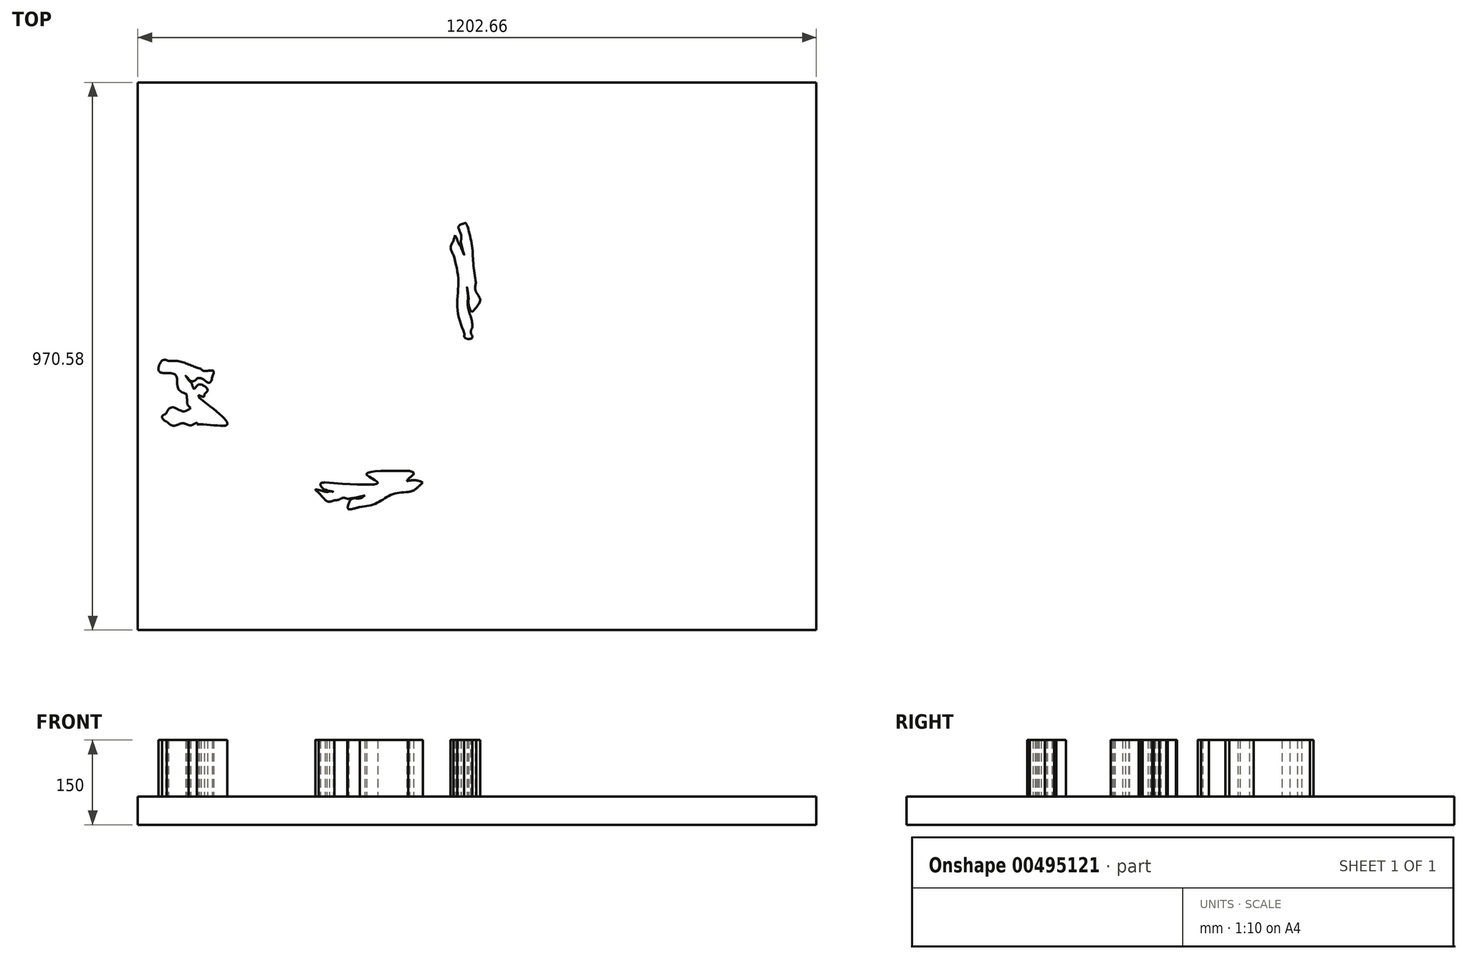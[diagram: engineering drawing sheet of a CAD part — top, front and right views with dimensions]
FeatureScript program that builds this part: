
annotation { "Feature Type Name" : "Feature", "Feature Type Description" : "" }
export const myFeature = defineFeature(function(context is Context, id is Id, definition is map)
    precondition{}
    {
        {
            var Q0;
            Q0=qCreatedBy(makeId("Top.planeOp"),FACE);
            var sketch = newSketch(context, id + "F0", { "sketchPlane" : qUnion([Q0])});
            skFitSpline(sketch, "E0", {"points": [v(381.94, 4384.72) * mm, v(61.51, 4229.76) * mm, v(-168.88, 3941.71) * mm, v(-376.86, 3662.72) * mm]});
            skFitSpline(sketch, "E1", {"points": [v(-376.86, 3662.72) * mm, v(-485.66, 3465.57) * mm, v(-439.05, 3228.77) * mm, v(-451.72, 3017.95) * mm]});
            skFitSpline(sketch, "E2", {"points": [v(-451.72, 3017.95) * mm, v(-592.53, 3305.6) * mm, v(-700.1, 3616.54) * mm, v(-908.92, 3864.94) * mm]});
            skFitSpline(sketch, "E3", {"points": [v(-908.92, 3864.94) * mm, v(-1055.94, 3885.93) * mm, v(-1192.81, 4049.02) * mm, v(-1345.32, 3977.6) * mm]});
            skFitSpline(sketch, "E4", {"points": [v(-1345.32, 3977.6) * mm, v(-1485.92, 3883.68) * mm, v(-1586.13, 3723.07) * mm, v(-1707.87, 3624.99) * mm]});
            skFitSpline(sketch, "E5", {"points": [v(-1707.87, 3624.99) * mm, v(-1881.76, 3746.23) * mm, v(-2092.76, 3809.04) * mm, v(-2303.44, 3807.45) * mm]});
            skFitSpline(sketch, "E6", {"points": [v(-2303.44, 3807.45) * mm, v(-2463.1, 3831.75) * mm, v(-2540.01, 3655.35) * mm, v(-2582.24, 3533.07) * mm]});
            skFitSpline(sketch, "E7", {"points": [v(-2582.24, 3533.07) * mm, v(-2664.53, 3358.6) * mm, v(-2728.63, 3164.85) * mm, v(-2728.12, 2973.38) * mm]});
            skFitSpline(sketch, "E8", {"points": [v(-2728.12, 2973.38) * mm, v(-2886.17, 2991.23) * mm, v(-3055.94, 3040.55) * mm, v(-3210.55, 2981.08) * mm]});
            skFitSpline(sketch, "E9", {"points": [v(-3210.55, 2981.08) * mm, v(-3401.65, 2854.65) * mm, v(-3465.48, 2610.22) * mm, v(-3512.5, 2398.13) * mm]});
            skFitSpline(sketch, "E10", {"points": [v(-3512.5, 2398.13) * mm, v(-3506.72, 2299.67) * mm, v(-3584.36, 2389.32) * mm, v(-3630.84, 2406.94) * mm]});
            skFitSpline(sketch, "E11", {"points": [v(-3630.84, 2406.94) * mm, v(-3726.37, 2462.26) * mm, v(-3829.3, 2509.52) * mm, v(-3940.07, 2522.47) * mm]});
            skFitSpline(sketch, "E12", {"points": [v(-3940.07, 2522.47) * mm, v(-4053.3, 2415.36) * mm, v(-4027.81, 2237.75) * mm, v(-4125.28, 2122.83) * mm]});
            skFitSpline(sketch, "E13", {"points": [v(-4125.28, 2122.83) * mm, v(-4228.2, 2164.5) * mm, v(-4337.02, 2185.35) * mm, v(-4446.82, 2165.54) * mm]});
            skFitSpline(sketch, "E14", {"points": [v(-4446.82, 2165.54) * mm, v(-4542.37, 2162.54) * mm, v(-4656.2, 2120.88) * mm, v(-4680.37, 2017.9) * mm]});
            skFitSpline(sketch, "E15", {"points": [v(-4680.37, 2017.9) * mm, v(-4768.24, 1961.3) * mm, v(-4837.09, 1871.01) * mm, v(-4826.86, 1762) * mm]});
            skFitSpline(sketch, "E16", {"points": [v(-4826.86, 1762) * mm, v(-4839.37, 1636.97) * mm, v(-4783.31, 1481.6) * mm, v(-4883.82, 1384.45) * mm]});
            skFitSpline(sketch, "E17", {"points": [v(-4883.82, 1384.45) * mm, v(-4993.4, 1355.95) * mm, v(-5135.64, 1257.94) * mm, v(-5076.6, 1127.43) * mm]});
            skFitSpline(sketch, "E18", {"points": [v(-5076.6, 1127.43) * mm, v(-5017, 810.29) * mm, v(-5048.65, 468.95) * mm, v(-4913.38, 170.07) * mm]});
            skFitSpline(sketch, "E19", {"points": [v(-4913.38, 170.07) * mm, v(-4537.22, -178.3) * mm, v(-4182.23, -760.02) * mm, v(-3843.25, -964.95) * mm]});
            skFitSpline(sketch, "E20", {"points": [v(-3843.25, -964.95) * mm, v(-3429.88, -1228.09) * mm, v(-3011.81, -1516.53) * mm, v(-2521.36, -1610.75) * mm]});
            skFitSpline(sketch, "E21", {"points": [v(-2521.36, -1610.75) * mm, v(-2223.74, -1687.78) * mm, v(-1916.74, -1742.89) * mm, v(-1608.11, -1721.51) * mm]});
            skFitSpline(sketch, "E22", {"points": [v(-1608.11, -1721.51) * mm, v(-1837.29, -1504.9) * mm, v(-2160.43, -1465.21) * mm, v(-2458.64, -1425.57) * mm]});
            skFitSpline(sketch, "E23", {"points": [v(-2458.64, -1425.57) * mm, v(-2571.55, -1397.31) * mm, v(-2715.84, -1404.33) * mm, v(-2786.2, -1296.98) * mm]});
            skFitSpline(sketch, "E24", {"points": [v(-2786.2, -1296.98) * mm, v(-2833.59, -1272.32) * mm, v(-2889.54, -1276.7) * mm, v(-2922.42, -1223.35) * mm]});
            skFitSpline(sketch, "E25", {"points": [v(-2922.42, -1223.35) * mm, v(-3056.81, -1147.33) * mm, v(-3214.24, -1070.95) * mm, v(-3333.03, -994.45) * mm]});
            skFitSpline(sketch, "E26", {"points": [v(-3333.03, -994.45) * mm, v(-2966.3, -1154.76) * mm, v(-2582.76, -1277.88) * mm, v(-2184.25, -1326.12) * mm]});
            skFitSpline(sketch, "E27", {"points": [v(-2184.25, -1326.12) * mm, v(-1899.07, -1372.45) * mm, v(-1606.28, -1412.61) * mm, v(-1339.78, -1524.4) * mm]});
            skFitSpline(sketch, "E28", {"points": [v(-1339.78, -1524.4) * mm, v(-1408.16, -1740.88) * mm, v(-1233.1, -1955.8) * mm, v(-1041.75, -2038) * mm]});
            skFitSpline(sketch, "E29", {"points": [v(-1041.75, -2038) * mm, v(-1020.89, -2064.7) * mm, v(-927.97, -2067.76) * mm, v(-989.47, -2094.22) * mm]});
            skFitSpline(sketch, "E30", {"points": [v(-989.47, -2094.22) * mm, v(-1018.06, -2158.05) * mm, v(-925.94, -2193.33) * mm, v(-891.77, -2231.51) * mm]});
            skFitSpline(sketch, "E31", {"points": [v(-891.77, -2231.51) * mm, v(-831.37, -2270.27) * mm, v(-715.35, -2235.91) * mm, v(-691.3, -2313.7) * mm]});
            skFitSpline(sketch, "E32", {"points": [v(-691.3, -2313.7) * mm, v(-737.42, -2394.05) * mm, v(-694.6, -2526.4) * mm, v(-586.67, -2510.53) * mm]});
            skFitSpline(sketch, "E33", {"points": [v(-586.67, -2510.53) * mm, v(-538.8, -2528.13) * mm, v(-497.63, -2454.43) * mm, v(-486.8, -2451.74) * mm]});
            skFitSpline(sketch, "E34", {"points": [v(-486.8, -2451.74) * mm, v(-453.58, -2534.78) * mm, v(-345.93, -2486.64) * mm, v(-315.32, -2427.44) * mm]});
            skFitSpline(sketch, "E35", {"points": [v(-315.32, -2427.44) * mm, v(-220.27, -2360.65) * mm, v(-103.97, -2405.84) * mm, v(-12.86, -2453.97) * mm]});
            skFitSpline(sketch, "E36", {"points": [v(-12.86, -2453.97) * mm, v(43.72, -2475.4) * mm, v(129.7, -2425.68) * mm, v(89.8, -2362.7) * mm]});
            skFitSpline(sketch, "E37", {"points": [v(89.8, -2362.7) * mm, v(142.8, -2371.8) * mm, v(205.28, -2375.75) * mm, v(251.83, -2350.76) * mm]});
            skFitSpline(sketch, "E38", {"points": [v(251.83, -2350.76) * mm, v(197.6, -2402.32) * mm, v(153.64, -2462.44) * mm, v(114.42, -2526.04) * mm]});
            skFitSpline(sketch, "E39", {"points": [v(114.42, -2526.04) * mm, v(232.2, -2500.92) * mm, v(371.66, -2458.59) * mm, v(452.49, -2377) * mm]});
            skFitSpline(sketch, "E40", {"points": [v(452.49, -2377) * mm, v(402.7, -2431.92) * mm, v(476.76, -2502.87) * mm, v(409.65, -2550.57) * mm]});
            skFitSpline(sketch, "E41", {"points": [v(409.65, -2550.57) * mm, v(301.85, -2846.94) * mm, v(450.9, -3206.12) * mm, v(247.03, -3474) * mm]});
            skFitSpline(sketch, "E42", {"points": [v(247.03, -3474) * mm, v(170.57, -3582.93) * mm, v(114.15, -3712.15) * mm, v(134.4, -3848.23) * mm]});
            skFitSpline(sketch, "E43", {"points": [v(134.4, -3848.23) * mm, v(309.33, -3710.03) * mm, v(459.4, -3530.37) * mm, v(553.73, -3330.2) * mm]});
            skFitSpline(sketch, "E44", {"points": [v(553.73, -3330.2) * mm, v(582.44, -3111.76) * mm, v(532.47, -2891.24) * mm, v(548.93, -2671.48) * mm]});
            skFitSpline(sketch, "E45", {"points": [v(548.93, -2671.48) * mm, v(556.04, -2618.71) * mm, v(529.26, -2548) * mm, v(538.25, -2506.77) * mm]});
            skFitSpline(sketch, "E46", {"points": [v(538.25, -2506.77) * mm, v(591.2, -2458.08) * mm, v(677.15, -2436.14) * mm, v(707.58, -2367.76) * mm]});
            skFitSpline(sketch, "E47", {"points": [v(707.58, -2367.76) * mm, v(719.75, -2310.82) * mm, v(622.82, -2316.92) * mm, v(620.4, -2312.4) * mm]});
            skFitSpline(sketch, "E48", {"points": [v(620.4, -2312.4) * mm, v(725.45, -2260.19) * mm, v(633.6, -2101.21) * mm, v(533.22, -2150.06) * mm]});
            skFitSpline(sketch, "E49", {"points": [v(533.22, -2150.06) * mm, v(486.69, -2157.75) * mm, v(457.8, -2232.15) * mm, v(419.78, -2169.23) * mm]});
            skFitSpline(sketch, "E50", {"points": [v(419.78, -2169.23) * mm, v(390.66, -2142.37) * mm, v(340.96, -2142.2) * mm, v(394.14, -2108.62) * mm]});
            skFitSpline(sketch, "E51", {"points": [v(394.14, -2108.62) * mm, v(451.5, -2055) * mm, v(423.9, -1905.48) * mm, v(326.95, -1954.8) * mm]});
            skFitSpline(sketch, "E52", {"points": [v(326.95, -1954.8) * mm, v(271.66, -1965.7) * mm, v(246.12, -2034.53) * mm, v(244.46, -2071.82) * mm]});
            skFitSpline(sketch, "E53", {"points": [v(244.46, -2071.82) * mm, v(152.83, -2015.1) * mm, v(8.64, -2032.45) * mm, v(-28.97, -2146.68) * mm]});
            skFitSpline(sketch, "E54", {"points": [v(-28.97, -2146.68) * mm, v(-39.36, -2193.37) * mm, v(-108.6, -2132.76) * mm, v(-142.5, -2150.77) * mm]});
            skFitSpline(sketch, "E55", {"points": [v(-142.5, -2150.77) * mm, v(-157.59, -2071.73) * mm, v(-288.17, -2236.29) * mm, v(-368.64, -2235.27) * mm]});
            skFitSpline(sketch, "E56", {"points": [v(-368.64, -2235.27) * mm, v(-345.16, -2147.34) * mm, v(-427.27, -2093.93) * mm, v(-507.16, -2098.35) * mm]});
            skFitSpline(sketch, "E57", {"points": [v(-507.16, -2098.35) * mm, v(-618.47, -2084.89) * mm, v(-756.71, -2107.9) * mm, v(-850.84, -2087.4) * mm]});
            skFitSpline(sketch, "E58", {"points": [v(-850.84, -2087.4) * mm, v(-578.06, -1867.53) * mm, v(-993.2, -1646.27) * mm, v(-1163.79, -1654.88) * mm]});
            skFitSpline(sketch, "E59", {"points": [v(-1163.79, -1654.88) * mm, v(-1189.81, -1639.65) * mm, v(-1251.4, -1549.4) * mm, v(-1186.49, -1600.26) * mm]});
            skFitSpline(sketch, "E60", {"points": [v(-1186.49, -1600.26) * mm, v(-1139.63, -1647.5) * mm, v(-1009.9, -1692.39) * mm, v(-1011.8, -1584.44) * mm]});
            skFitSpline(sketch, "E61", {"points": [v(-1011.8, -1584.44) * mm, v(-1019.86, -1505.94) * mm, v(-948, -1427.16) * mm, v(-988.66, -1345.28) * mm]});
            skFitSpline(sketch, "E62", {"points": [v(-988.66, -1345.28) * mm, v(-1031.89, -1228.57) * mm, v(-1184.07, -1291.47) * mm, v(-1260.56, -1231.87) * mm]});
            skFitSpline(sketch, "E63", {"points": [v(-1260.56, -1231.87) * mm, v(-1144.18, -1228.8) * mm, v(-1037.49, -1177.44) * mm, v(-921.31, -1171) * mm]});
            skFitSpline(sketch, "E64", {"points": [v(-921.31, -1171) * mm, v(-1005.32, -1039.9) * mm, v(-1107.66, -1001.5) * mm, v(-1250.9, -938.46) * mm]});
            skFitSpline(sketch, "E65", {"points": [v(-1250.9, -938.46) * mm, v(-1235.63, -884.1) * mm, v(-1168.7, -884.8) * mm, v(-1144.4, -883.2) * mm]});
            skFitSpline(sketch, "E66", {"points": [v(-1144.4, -883.2) * mm, v(-1075.39, -939.3) * mm, v(-931.82, -992.61) * mm, v(-883.4, -893.06) * mm]});
            skFitSpline(sketch, "E67", {"points": [v(-883.4, -893.06) * mm, v(-863.05, -857.83) * mm, v(-893, -747.84) * mm, v(-825.43, -782.07) * mm]});
            skFitSpline(sketch, "E68", {"points": [v(-825.43, -782.07) * mm, v(-732.06, -805.46) * mm, v(-646.47, -726.95) * mm, v(-636.75, -636.86) * mm]});
            skFitSpline(sketch, "E69", {"points": [v(-636.75, -636.86) * mm, v(-623.52, -605.26) * mm, v(-595.46, -488.49) * mm, v(-562.15, -561.85) * mm]});
            skFitSpline(sketch, "E70", {"points": [v(-562.15, -561.85) * mm, v(-483.19, -649.38) * mm, v(-350.67, -567.19) * mm, v(-332.92, -468.05) * mm]});
            skFitSpline(sketch, "E71", {"points": [v(-332.92, -468.05) * mm, v(-327.52, -397.06) * mm, v(-277.23, -335.5) * mm, v(-199.75, -366.36) * mm]});
            skFitSpline(sketch, "E72", {"points": [v(-199.75, -366.36) * mm, v(-120.15, -381.79) * mm, v(-43.71, -412.05) * mm, v(37.96, -417.3) * mm]});
            skFitSpline(sketch, "E73", {"points": [v(37.96, -417.3) * mm, v(14.09, -384.65) * mm, v(29.35, -312.71) * mm, v(57.53, -368.93) * mm]});
            skFitSpline(sketch, "E74", {"points": [v(57.53, -368.93) * mm, v(70.46, -466.02) * mm, v(197.51, -455.45) * mm, v(247.29, -392.48) * mm]});
            skFitSpline(sketch, "E75", {"points": [v(247.29, -392.48) * mm, v(305.25, -336.01) * mm, v(456.4, -297.69) * mm, v(491.14, -392.36) * mm]});
            skFitSpline(sketch, "E76", {"points": [v(491.14, -392.36) * mm, v(462.37, -433.43) * mm, v(444.51, -524.25) * mm, v(521.24, -524.49) * mm]});
            skFitSpline(sketch, "E77", {"points": [v(521.24, -524.49) * mm, v(595.54, -525.52) * mm, v(695.8, -611.72) * mm, v(753.42, -515.07) * mm]});
            skFitSpline(sketch, "E78", {"points": [v(753.42, -515.07) * mm, v(780.5, -478.65) * mm, v(787.2, -432.33) * mm, v(808.56, -393.03) * mm]});
            skFitSpline(sketch, "E79", {"points": [v(808.56, -393.03) * mm, v(839.14, -517.72) * mm, v(863.54, -696.53) * mm, v(1005.8, -738.61) * mm]});
            skFitSpline(sketch, "E80", {"points": [v(1005.8, -738.61) * mm, v(1064.64, -746.16) * mm, v(1144.59, -712.74) * mm, v(1185.46, -718.63) * mm]});
            skFitSpline(sketch, "E81", {"points": [v(1185.46, -718.63) * mm, v(1088.84, -732.37) * mm, v(998.24, -810.44) * mm, v(1019.67, -915.87) * mm]});
            skFitSpline(sketch, "E82", {"points": [v(1019.67, -915.87) * mm, v(1025.37, -1038.38) * mm, v(1181.98, -1163.79) * mm, v(1287.3, -1065.33) * mm]});
            skFitSpline(sketch, "E83", {"points": [v(1287.3, -1065.33) * mm, v(1316.93, -993.48) * mm, v(1406.21, -948.4) * mm, v(1462.4, -1017.33) * mm]});
            skFitSpline(sketch, "E84", {"points": [v(1462.4, -1017.33) * mm, v(1499.04, -1033.64) * mm, v(1536.51, -1023.95) * mm, v(1521.1, -1074.7) * mm]});
            skFitSpline(sketch, "E85", {"points": [v(1521.1, -1074.7) * mm, v(1546.18, -1120.1) * mm, v(1458.99, -1072.03) * mm, v(1438.55, -1109.8) * mm]});
            skFitSpline(sketch, "E86", {"points": [v(1438.55, -1109.8) * mm, v(1358.69, -1171.56) * mm, v(1350.95, -1312.85) * mm, v(1235.17, -1326.3) * mm]});
            skFitSpline(sketch, "E87", {"points": [v(1235.17, -1326.3) * mm, v(1137.9, -1399.68) * mm, v(1100.96, -1606.85) * mm, v(1248.94, -1643.86) * mm]});
            skFitSpline(sketch, "E88", {"points": [v(1248.94, -1643.86) * mm, v(1391.6, -1652.84) * mm, v(1457.61, -1496.4) * mm, v(1548.42, -1415.11) * mm]});
            skFitSpline(sketch, "E89", {"points": [v(1548.42, -1415.11) * mm, v(1526.21, -1462.61) * mm, v(1639.8, -1411.02) * mm, v(1679.09, -1404.92) * mm]});
            skFitSpline(sketch, "E90", {"points": [v(1679.09, -1404.92) * mm, v(1858.67, -1333.85) * mm, v(2016.76, -1218.63) * mm, v(2188.38, -1131.07) * mm]});
            skFitSpline(sketch, "E91", {"points": [v(2188.38, -1131.07) * mm, v(2270.2, -1086.94) * mm, v(2356.38, -1004.92) * mm, v(2424.94, -967.88) * mm]});
            skFitSpline(sketch, "E92", {"points": [v(2424.94, -967.88) * mm, v(2472.06, -1013.58) * mm, v(2374.24, -1013.3) * mm, v(2347.77, -1043.3) * mm]});
            skFitSpline(sketch, "E93", {"points": [v(2347.77, -1043.3) * mm, v(2140.92, -1175.72) * mm, v(1974.96, -1376.96) * mm, v(1728.1, -1440.64) * mm]});
            skFitSpline(sketch, "E94", {"points": [v(1728.1, -1440.64) * mm, v(1558.12, -1488.51) * mm, v(1390.74, -1572.7) * mm, v(1296.82, -1729.47) * mm]});
            skFitSpline(sketch, "E95", {"points": [v(1296.82, -1729.47) * mm, v(1166.76, -1603.78) * mm, v(934.6, -1759.88) * mm, v(941.87, -1910.67) * mm]});
            skFitSpline(sketch, "E96", {"points": [v(941.87, -1910.67) * mm, v(541.52, -1709.25) * mm, v(598.27, -2308.63) * mm, v(842.38, -2193.04) * mm]});
            skFitSpline(sketch, "E97", {"points": [v(842.38, -2193.04) * mm, v(907.53, -2150.42) * mm, v(971.59, -2075.63) * mm, v(981.83, -2003.47) * mm]});
            skFitSpline(sketch, "E98", {"points": [v(981.83, -2003.47) * mm, v(1042.68, -2075.03) * mm, v(1158.94, -2062.05) * mm, v(1223.75, -2002.09) * mm]});
            skFitSpline(sketch, "E99", {"points": [v(1223.75, -2002.09) * mm, v(1140.14, -2448.86) * mm, v(1159.14, -2192.78) * mm, v(738.8, -2432.76) * mm]});
            skFitSpline(sketch, "E100", {"points": [v(738.8, -2432.76) * mm, v(898.93, -2514.9) * mm, v(1082.24, -2525.88) * mm, v(1253.1, -2570.58) * mm]});
            skFitSpline(sketch, "E101", {"points": [v(1253.1, -2570.58) * mm, v(1313.17, -2580.5) * mm, v(1291.93, -2488.08) * mm, v(1350.51, -2524.44) * mm]});
            skFitSpline(sketch, "E102", {"points": [v(1350.51, -2524.44) * mm, v(1455.09, -2537.37) * mm, v(1601.02, -2530.2) * mm, v(1640.36, -2651.24) * mm]});
            skFitSpline(sketch, "E103", {"points": [v(1640.36, -2651.24) * mm, v(1725.72, -2726.43) * mm, v(1846.9, -2651.65) * mm, v(1946.6, -2668.58) * mm]});
            skFitSpline(sketch, "E104", {"points": [v(1946.6, -2668.58) * mm, v(2363.71, -2658.06) * mm, v(2798.95, -2809.82) * mm, v(3204.28, -2657) * mm]});
            skFitSpline(sketch, "E105", {"points": [v(3204.28, -2657) * mm, v(3272.1, -2588.5) * mm, v(3151.38, -2545.86) * mm, v(3096.16, -2544.83) * mm]});
            skFitSpline(sketch, "E106", {"points": [v(3096.16, -2544.83) * mm, v(2835.02, -2517.43) * mm, v(2568.1, -2524.52) * mm, v(2325.3, -2408.32) * mm]});
            skFitSpline(sketch, "E107", {"points": [v(2325.3, -2408.32) * mm, v(2236.94, -2392.75) * mm, v(2376.56, -2398.94) * mm, v(2412.59, -2397.8) * mm]});
            skFitSpline(sketch, "E108", {"points": [v(2412.59, -2397.8) * mm, v(2745.1, -2395.01) * mm, v(3087.04, -2476.03) * mm, v(3419.22, -2413.19) * mm]});
            skFitSpline(sketch, "E109", {"points": [v(3419.22, -2413.19) * mm, v(3734, -2367.32) * mm, v(3527.64, -2318.48) * mm, v(3514.62, -2582.7) * mm]});
            skFitSpline(sketch, "E110", {"points": [v(3514.62, -2582.7) * mm, v(3463.42, -2696.5) * mm, v(3333.66, -2775.48) * mm, v(3300.05, -2890.1) * mm]});
            skFitSpline(sketch, "E111", {"points": [v(3300.05, -2890.1) * mm, v(2067.15, -3164.09) * mm, v(1999.97, -4139.85) * mm, v(2702.59, -3302.99) * mm]});
            skFitSpline(sketch, "E112", {"points": [v(2702.59, -3302.99) * mm, v(2755.9, -3214.98) * mm, v(2860.1, -3289.2) * mm, v(2940.04, -3257.23) * mm]});
            skFitSpline(sketch, "E113", {"points": [v(2940.04, -3257.23) * mm, v(3129.92, -3222.36) * mm, v(3299.57, -3113.32) * mm, v(3469.42, -3036.15) * mm]});
            skFitSpline(sketch, "E114", {"points": [v(3469.42, -3036.15) * mm, v(3524.46, -2958.06) * mm, v(3529.47, -2847.82) * mm, v(3623.79, -2801) * mm]});
            skFitSpline(sketch, "E115", {"points": [v(3623.79, -2801) * mm, v(3719.98, -2714.4) * mm, v(3756.82, -2581.22) * mm, v(3745.12, -2456.5) * mm]});
            skFitSpline(sketch, "E116", {"points": [v(3745.12, -2456.5) * mm, v(3796.05, -2358.5) * mm, v(3925.66, -2343.44) * mm, v(3997.05, -2261.76) * mm]});
            skFitSpline(sketch, "E117", {"points": [v(3997.05, -2261.76) * mm, v(4227.5, -2084.35) * mm, v(4371.9, -1809.14) * mm, v(4393.55, -1519.74) * mm]});
            skFitSpline(sketch, "E118", {"points": [v(4393.55, -1519.74) * mm, v(4455.42, -1206) * mm, v(4488.61, -884.11) * mm, v(4463.63, -565.6) * mm]});
            skFitSpline(sketch, "E119", {"points": [v(4463.63, -565.6) * mm, v(4516.98, -451.04) * mm, v(4633.98, -381.35) * mm, v(4712.12, -284.23) * mm]});
            skFitSpline(sketch, "E120", {"points": [v(4712.12, -284.23) * mm, v(5008.28, 9) * mm, v(5358.22, 268.05) * mm, v(5583.63, 623.5) * mm]});
            skFitSpline(sketch, "E121", {"points": [v(5583.63, 623.5) * mm, v(5608.93, 736.72) * mm, v(5466.77, 765.53) * mm, v(5388.7, 775.56) * mm]});
            skFitSpline(sketch, "E122", {"points": [v(5388.7, 775.56) * mm, v(5223.7, 808.86) * mm, v(5043.31, 879.82) * mm, v(4877.6, 818.65) * mm]});
            skFitSpline(sketch, "E123", {"points": [v(4877.6, 818.65) * mm, v(4668.85, 693.96) * mm, v(4644.24, 409.7) * mm, v(4453.47, 264.04) * mm]});
            skFitSpline(sketch, "E124", {"points": [v(4453.47, 264.04) * mm, v(4317.57, 168.13) * mm, v(4160.83, 97.6) * mm, v(4051.11, -32.94) * mm]});
            skFitSpline(sketch, "E125", {"points": [v(4051.11, -32.94) * mm, v(3972.01, -113.43) * mm, v(3927.33, -239.29) * mm, v(3932.83, -341.76) * mm]});
            skFitSpline(sketch, "E126", {"points": [v(3932.83, -341.76) * mm, v(3858.05, -304.79) * mm, v(3761.66, -379.37) * mm, v(3678.13, -391.64) * mm]});
            skFitSpline(sketch, "E127", {"points": [v(3678.13, -391.64) * mm, v(3432.87, -468.8) * mm, v(3189.34, -551.41) * mm, v(2947.59, -638.9) * mm]});
            skFitSpline(sketch, "E128", {"points": [v(2947.59, -638.9) * mm, v(3498.14, -303.37) * mm, v(4051.7, 125.3) * mm, v(4283.2, 749.93) * mm]});
            skFitSpline(sketch, "E129", {"points": [v(4283.2, 749.93) * mm, v(4366.95, 959.65) * mm, v(4361.41, 1188.76) * mm, v(4323.47, 1407.36) * mm]});
            skFitSpline(sketch, "E130", {"points": [v(4323.47, 1407.36) * mm, v(4306.82, 1509.4) * mm, v(4301.7, 1633.67) * mm, v(4402.5, 1693.35) * mm]});
            skFitSpline(sketch, "E131", {"points": [v(4402.5, 1693.35) * mm, v(4538.68, 1841.58) * mm, v(4601.69, 2041.1) * mm, v(4663.73, 2228.61) * mm]});
            skFitSpline(sketch, "E132", {"points": [v(4663.73, 2228.61) * mm, v(4681.22, 2332.4) * mm, v(4721.15, 2497.7) * mm, v(4600.21, 2550.53) * mm]});
            skFitSpline(sketch, "E133", {"points": [v(4600.21, 2550.53) * mm, v(4523.14, 2579.13) * mm, v(4439.2, 2520.6) * mm, v(4381.58, 2495.76) * mm]});
            skFitSpline(sketch, "E134", {"points": [v(4381.58, 2495.76) * mm, v(4435.17, 2643.92) * mm, v(4398.33, 2803) * mm, v(4392.52, 2955.41) * mm]});
            skFitSpline(sketch, "E135", {"points": [v(4392.52, 2955.41) * mm, v(4243.25, 2994.85) * mm, v(4065.67, 2917.7) * mm, v(3936.1, 3002.7) * mm]});
            skFitSpline(sketch, "E136", {"points": [v(3936.1, 3002.7) * mm, v(3925.06, 3159.06) * mm, v(3946.07, 3330.65) * mm, v(3851.87, 3467.53) * mm]});
            skFitSpline(sketch, "E137", {"points": [v(3851.87, 3467.53) * mm, v(3549.75, 3274.7) * mm, v(3318.5, 2995.09) * mm, v(3098.31, 2717.18) * mm]});
            skFitSpline(sketch, "E138", {"points": [v(3098.31, 2717.18) * mm, v(3148.8, 2940.46) * mm, v(3156.09, 3191.64) * mm, v(3017.95, 3386.72) * mm]});
            skFitSpline(sketch, "E139", {"points": [v(3017.95, 3386.72) * mm, v(2960.27, 3501.2) * mm, v(2936.36, 3650.65) * mm, v(2831.91, 3731.77) * mm]});
            skFitSpline(sketch, "E140", {"points": [v(2831.91, 3731.77) * mm, v(2600.97, 3799.14) * mm, v(2352.54, 3680.63) * mm, v(2131.27, 3775.5) * mm]});
            skFitSpline(sketch, "E141", {"points": [v(2131.27, 3775.5) * mm, v(2040.27, 3871.32) * mm, v(1966.17, 3992.56) * mm, v(1839.71, 4045.17) * mm]});
            skFitSpline(sketch, "E142", {"points": [v(1839.71, 4045.17) * mm, v(1764.9, 4138.61) * mm, v(1763, 4318.38) * mm, v(1616.06, 4336.98) * mm]});
            skFitSpline(sketch, "E143", {"points": [v(1616.06, 4336.98) * mm, v(1348.79, 4366.65) * mm, v(1185.71, 4049.14) * mm, v(919.95, 4084.76) * mm]});
            skFitSpline(sketch, "E144", {"points": [v(919.95, 4084.76) * mm, v(722.34, 4144.08) * mm, v(589.4, 4363.1) * mm, v(381.94, 4384.72) * mm]});
            skFitSpline(sketch, "E145", {"points": [v(424.13, 4170.81) * mm, v(596.15, 4073.7) * mm, v(721.2, 3876.6) * mm, v(937.37, 3870.26) * mm]});
            skFitSpline(sketch, "E146", {"points": [v(937.37, 3870.26) * mm, v(1186.08, 3855.25) * mm, v(1372, 4067.61) * mm, v(1574.84, 4164.75) * mm]});
            skFitSpline(sketch, "E147", {"points": [v(1574.84, 4164.75) * mm, v(1605.7, 4020.68) * mm, v(1676.47, 3867.38) * mm, v(1823.86, 3813.25) * mm]});
            skFitSpline(sketch, "E148", {"points": [v(1823.86, 3813.25) * mm, v(1933.6, 3714.57) * mm, v(2028.46, 3534.15) * mm, v(2205.12, 3560.17) * mm]});
            skFitSpline(sketch, "E149", {"points": [v(2205.12, 3560.17) * mm, v(2384.17, 3560.37) * mm, v(2601, 3629.18) * mm, v(2745.18, 3487.92) * mm]});
            skFitSpline(sketch, "E150", {"points": [v(2745.18, 3487.92) * mm, v(2773.31, 3398.67) * mm, v(2799.73, 3304.8) * mm, v(2877.57, 3245.03) * mm]});
            skFitSpline(sketch, "E151", {"points": [v(2877.57, 3245.03) * mm, v(2992.06, 3079.6) * mm, v(2921.67, 2863.52) * mm, v(2900.08, 2681.76) * mm]});
            skFitSpline(sketch, "E152", {"points": [v(2900.08, 2681.76) * mm, v(2893.18, 2220.34) * mm, v(2596.9, 2016.57) * mm, v(2479.38, 1691.41) * mm]});
            skFitSpline(sketch, "E153", {"points": [v(2479.38, 1691.41) * mm, v(2452.39, 1623.9) * mm, v(2534.44, 1565.65) * mm, v(2583.3, 1623.8) * mm]});
            skFitSpline(sketch, "E154", {"points": [v(2583.3, 1623.8) * mm, v(2524, 1451.93) * mm, v(2473.4, 1261.7) * mm, v(2328.5, 1144.32) * mm]});
            skFitSpline(sketch, "E155", {"points": [v(2328.5, 1144.32) * mm, v(2287.38, 1101.55) * mm, v(2300.7, 1033.32) * mm, v(2327.65, 996.05) * mm]});
            skFitSpline(sketch, "E156", {"points": [v(2327.65, 996.05) * mm, v(2270.45, 960.2) * mm, v(2232.54, 907.05) * mm, v(2228.34, 839.15) * mm]});
            skFitSpline(sketch, "E157", {"points": [v(2228.34, 839.15) * mm, v(2128.23, 595.9) * mm, v(1919.68, 420.83) * mm, v(1753.46, 223.71) * mm]});
            skFitSpline(sketch, "E158", {"points": [v(1753.46, 223.71) * mm, v(1600.01, 72.18) * mm, v(1442.05, -83.2) * mm, v(1349.62, -280.52) * mm]});
            skFitSpline(sketch, "E159", {"points": [v(1349.62, -280.52) * mm, v(1276.5, -358.07) * mm, v(1225.41, -450.4) * mm, v(1181.4, -544.84) * mm]});
            skFitSpline(sketch, "E160", {"points": [v(1181.4, -544.84) * mm, v(1157.72, -474.27) * mm, v(1200.64, -383.45) * mm, v(1169.2, -308.1) * mm]});
            skFitSpline(sketch, "E161", {"points": [v(1169.2, -308.1) * mm, v(1282.85, -136.75) * mm, v(1493.58, -22.7) * mm, v(1526.4, 196.8) * mm]});
            skFitSpline(sketch, "E162", {"points": [v(1526.4, 196.8) * mm, v(1501.15, 224.85) * mm, v(1436.54, 185.17) * mm, v(1429.28, 202.72) * mm]});
            skFitSpline(sketch, "E163", {"points": [v(1429.28, 202.72) * mm, v(1427.21, 294.05) * mm, v(1303.47, 276.32) * mm, v(1274.69, 208.86) * mm]});
            skFitSpline(sketch, "E164", {"points": [v(1274.69, 208.86) * mm, v(1185.94, 107.67) * mm, v(1117.72, -72.94) * mm, v(955.64, -50.62) * mm]});
            skFitSpline(sketch, "E165", {"points": [v(955.64, -50.62) * mm, v(886.51, -61.04) * mm, v(852.5, -132.32) * mm, v(825, -186.61) * mm]});
            skFitSpline(sketch, "E166", {"points": [v(825, -186.61) * mm, v(802.49, -150.28) * mm, v(719.04, -170.48) * mm, v(743.74, -121.13) * mm]});
            skFitSpline(sketch, "E167", {"points": [v(743.74, -121.13) * mm, v(724.57, -46.45) * mm, v(687.42, 59.5) * mm, v(589.44, 50.25) * mm]});
            skFitSpline(sketch, "E168", {"points": [v(589.44, 50.25) * mm, v(484.12, 63.64) * mm, v(363.62, -24.76) * mm, v(393.44, -139.58) * mm]});
            skFitSpline(sketch, "E169", {"points": [v(393.44, -139.58) * mm, v(414.47, -180.89) * mm, v(395.66, -210.43) * mm, v(353.89, -167.9) * mm]});
            skFitSpline(sketch, "E170", {"points": [v(353.89, -167.9) * mm, v(264.03, -78.15) * mm, v(269.2, 64.03) * mm, v(194.2, 165.67) * mm]});
            skFitSpline(sketch, "E171", {"points": [v(194.2, 165.67) * mm, v(138.42, 274.38) * mm, v(135.78, 432.44) * mm, v(24.75, 502.83) * mm]});
            skFitSpline(sketch, "E172", {"points": [v(24.75, 502.83) * mm, v(-59.14, 528.8) * mm, v(-111.3, 423.35) * mm, v(-74.33, 356.5) * mm]});
            skFitSpline(sketch, "E173", {"points": [v(-74.33, 356.5) * mm, v(-67.57, 236.22) * mm, v(0.38, 100.36) * mm, v(62.18, 19.74) * mm]});
            skFitSpline(sketch, "E174", {"points": [v(62.18, 19.74) * mm, v(-16.63, 35.57) * mm, v(-62.9, 193.97) * mm, v(-152.35, 134.4) * mm]});
            skFitSpline(sketch, "E175", {"points": [v(-152.35, 134.4) * mm, v(-191.27, 102.43) * mm, v(-116.17, -11.3) * mm, v(-176.83, 51.29) * mm]});
            skFitSpline(sketch, "E176", {"points": [v(-176.83, 51.29) * mm, v(-255.68, 91.65) * mm, v(-317.06, -9.28) * mm, v(-290.46, -80.31) * mm]});
            skFitSpline(sketch, "E177", {"points": [v(-290.46, -80.31) * mm, v(-276.62, -108.51) * mm, v(-284.1, -205.76) * mm, v(-321.64, -186.32) * mm]});
            skFitSpline(sketch, "E178", {"points": [v(-321.64, -186.32) * mm, v(-299.8, -83.81) * mm, v(-387.83, 46.5) * mm, v(-501.8, -0.91) * mm]});
            skFitSpline(sketch, "E179", {"points": [v(-501.8, -0.91) * mm, v(-660.63, -29.96) * mm, v(-664.93, -233.77) * mm, v(-691.63, -342.66) * mm]});
            skFitSpline(sketch, "E180", {"points": [v(-691.63, -342.66) * mm, v(-746.75, -266.04) * mm, v(-830.54, -147.87) * mm, v(-941.96, -198.37) * mm]});
            skFitSpline(sketch, "E181", {"points": [v(-941.96, -198.37) * mm, v(-1007.24, -224.86) * mm, v(-1041.9, -299.38) * mm, v(-1028.58, -367.07) * mm]});
            skFitSpline(sketch, "E182", {"points": [v(-1028.58, -367.07) * mm, v(-1168.98, -250.76) * mm, v(-1303.42, -100.16) * mm, v(-1493.07, -70.53) * mm]});
            skFitSpline(sketch, "E183", {"points": [v(-1493.07, -70.53) * mm, v(-1926.88, 280.7) * mm, v(-2283.01, 715.44) * mm, v(-2682.2, 1101.6) * mm]});
            skFitSpline(sketch, "E184", {"points": [v(-2682.2, 1101.6) * mm, v(-2734.7, 1151.07) * mm, v(-2815.28, 1092.47) * mm, v(-2778.42, 1028.72) * mm]});
            skFitSpline(sketch, "E185", {"points": [v(-2778.42, 1028.72) * mm, v(-2692.35, 848.88) * mm, v(-2521.66, 726.9) * mm, v(-2409.26, 563.9) * mm]});
            skFitSpline(sketch, "E186", {"points": [v(-2409.26, 563.9) * mm, v(-2296.78, 441.6) * mm, v(-2214.88, 256.48) * mm, v(-2107.62, 158.18) * mm]});
            skFitSpline(sketch, "E187", {"points": [v(-2107.62, 158.18) * mm, v(-2560.88, 570.13) * mm, v(-3055.87, 992.43) * mm, v(-3268.03, 1582.66) * mm]});
            skFitSpline(sketch, "E188", {"points": [v(-3268.03, 1582.66) * mm, v(-3341.67, 1763.54) * mm, v(-3413.22, 1949.8) * mm, v(-3523.38, 2111.26) * mm]});
            skFitSpline(sketch, "E189", {"points": [v(-3523.38, 2111.26) * mm, v(-3393.81, 2089.67) * mm, v(-3356.07, 2248.69) * mm, v(-3342.52, 2344.5) * mm]});
            skFitSpline(sketch, "E190", {"points": [v(-3342.52, 2344.5) * mm, v(-3318.54, 2535.4) * mm, v(-3223.05, 2779.8) * mm, v(-3003.53, 2800.95) * mm]});
            skFitSpline(sketch, "E191", {"points": [v(-3003.53, 2800.95) * mm, v(-2862.66, 2807.17) * mm, v(-2716.92, 2823.72) * mm, v(-2578.96, 2821.58) * mm]});
            skFitSpline(sketch, "E192", {"points": [v(-2578.96, 2821.58) * mm, v(-2547.47, 2547.07) * mm, v(-2297.97, 2344.02) * mm, v(-2129.01, 2125.4) * mm]});
            skFitSpline(sketch, "E193", {"points": [v(-2129.01, 2125.4) * mm, v(-2062.96, 2060) * mm, v(-1992.09, 2005.5) * mm, v(-2029.3, 2142.4) * mm]});
            skFitSpline(sketch, "E194", {"points": [v(-2029.3, 2142.4) * mm, v(-2059.84, 2375.73) * mm, v(-2219.93, 2548.97) * mm, v(-2310.05, 2760.74) * mm]});
            skFitSpline(sketch, "E195", {"points": [v(-2310.05, 2760.74) * mm, v(-2380.04, 2905.66) * mm, v(-2482.92, 3076.12) * mm, v(-2516.56, 3223.52) * mm]});
            skFitSpline(sketch, "E196", {"points": [v(-2516.56, 3223.52) * mm, v(-2421.72, 3286.15) * mm, v(-2446.12, 3423.56) * mm, v(-2380.09, 3509.12) * mm]});
            skFitSpline(sketch, "E197", {"points": [v(-2380.09, 3509.12) * mm, v(-2336.51, 3617.94) * mm, v(-2210.91, 3662.47) * mm, v(-2110.3, 3604.04) * mm]});
            skFitSpline(sketch, "E198", {"points": [v(-2110.3, 3604.04) * mm, v(-1965.6, 3549.62) * mm, v(-1807.5, 3494.32) * mm, v(-1691.8, 3393.34) * mm]});
            skFitSpline(sketch, "E199", {"points": [v(-1691.8, 3393.34) * mm, v(-1700.5, 3332.38) * mm, v(-1512.66, 3260.4) * mm, v(-1521.68, 3321.3) * mm]});
            skFitSpline(sketch, "E200", {"points": [v(-1521.68, 3321.3) * mm, v(-1515.27, 3463.48) * mm, v(-1558.37, 3264.1) * mm, v(-1331.67, 3697.13) * mm]});
            skFitSpline(sketch, "E201", {"points": [v(-1331.67, 3697.13) * mm, v(-1285.52, 3791.04) * mm, v(-1176.8, 3786.58) * mm, v(-1103.21, 3732.74) * mm]});
            skFitSpline(sketch, "E202", {"points": [v(-1103.21, 3732.74) * mm, v(-897.43, 3640.52) * mm, v(-841.17, 3394.66) * mm, v(-741.73, 3212.4) * mm]});
            skFitSpline(sketch, "E203", {"points": [v(-741.73, 3212.4) * mm, v(-622.42, 2924.97) * mm, v(-487.6, 2641.92) * mm, v(-417.82, 2339.82) * mm]});
            skFitSpline(sketch, "E204", {"points": [v(-417.82, 2339.82) * mm, v(-358.39, 2362.96) * mm, v(-290.03, 2504.85) * mm, v(-228.8, 2404.7) * mm]});
            skFitSpline(sketch, "E205", {"points": [v(-228.8, 2404.7) * mm, v(-197.31, 2380.38) * mm, v(-185.2, 2477.56) * mm, v(-184.5, 2513.06) * mm]});
            skFitSpline(sketch, "E206", {"points": [v(-184.5, 2513.06) * mm, v(-191.01, 2615.85) * mm, v(-292.42, 2685.05) * mm, v(-267.27, 2795) * mm]});
            skFitSpline(sketch, "E207", {"points": [v(-267.27, 2795) * mm, v(-281.96, 3085.28) * mm, v(-330.26, 3413.77) * mm, v(-138.66, 3662.68) * mm]});
            skFitSpline(sketch, "E208", {"points": [v(-138.66, 3662.68) * mm, v(9.76, 3863.25) * mm, v(202.1, 4036.32) * mm, v(410.37, 4169.4) * mm]});
            skFitSpline(sketch, "E209", {"points": [v(410.37, 4169.4) * mm, v(414.89, 4170.35) * mm, v(419.51, 4170.83) * mm, v(424.13, 4170.81) * mm]});
            skFitSpline(sketch, "E210", {"points": [v(3748.66, 3116.26) * mm, v(3766.99, 3007.6) * mm, v(3695.47, 2844.86) * mm, v(3829.95, 2786.12) * mm]});
            skFitSpline(sketch, "E211", {"points": [v(3829.95, 2786.12) * mm, v(3963.4, 2726.72) * mm, v(4126.55, 2842.23) * mm, v(4245.15, 2744.67) * mm]});
            skFitSpline(sketch, "E212", {"points": [v(4245.15, 2744.67) * mm, v(4278.06, 2659.14) * mm, v(4185.74, 2579.58) * mm, v(4166.86, 2496.65) * mm]});
            skFitSpline(sketch, "E213", {"points": [v(4166.86, 2496.65) * mm, v(4126.19, 2419.71) * mm, v(4130.35, 2326.54) * mm, v(4120.95, 2247.88) * mm]});
            skFitSpline(sketch, "E214", {"points": [v(4120.95, 2247.88) * mm, v(4048.57, 2181.2) * mm, v(3958.2, 2100.93) * mm, v(3982.73, 1990.48) * mm]});
            skFitSpline(sketch, "E215", {"points": [v(3982.73, 1990.48) * mm, v(3985.56, 1718.1) * mm, v(4200.08, 1489.48) * mm, v(4159.87, 1211.3) * mm]});
            skFitSpline(sketch, "E216", {"points": [v(4159.87, 1211.3) * mm, v(4142.44, 654.23) * mm, v(3770.55, 179.58) * mm, v(3334.5, -134.67) * mm]});
            skFitSpline(sketch, "E217", {"points": [v(3334.5, -134.67) * mm, v(3094.96, -325.42) * mm, v(2814.03, -457.14) * mm, v(2566.81, -634.62) * mm]});
            skFitSpline(sketch, "E218", {"points": [v(2566.81, -634.62) * mm, v(2526.88, -681.33) * mm, v(2495.81, -781) * mm, v(2420.07, -732.07) * mm]});
            skFitSpline(sketch, "E219", {"points": [v(2420.07, -732.07) * mm, v(2425.33, -702.17) * mm, v(2516.4, -654.66) * mm, v(2555.56, -620.4) * mm]});
            skFitSpline(sketch, "E220", {"points": [v(2555.56, -620.4) * mm, v(2918.6, -369.96) * mm, v(3320.38, -125.43) * mm, v(3526.19, 282.34) * mm]});
            skFitSpline(sketch, "E221", {"points": [v(3526.19, 282.34) * mm, v(3602.72, 448.85) * mm, v(3737.03, 581.42) * mm, v(3812.17, 747.2) * mm]});
            skFitSpline(sketch, "E222", {"points": [v(3812.17, 747.2) * mm, v(3862.74, 954.46) * mm, v(3124.18, 294.46) * mm, v(3336.03, 319.55) * mm]});
            skFitSpline(sketch, "E223", {"points": [v(3336.03, 319.55) * mm, v(3251.87, 174.47) * mm, v(3158.46, 17.1) * mm, v(3012.96, -64.42) * mm]});
            skFitSpline(sketch, "E224", {"points": [v(3012.96, -64.42) * mm, v(2977.99, 16.36) * mm, v(2871.52, -24.49) * mm, v(2840.25, -87.53) * mm]});
            skFitSpline(sketch, "E225", {"points": [v(2840.25, -87.53) * mm, v(2469.19, -459.39) * mm, v(2016.78, -748.2) * mm, v(1526.35, -935.44) * mm]});
            skFitSpline(sketch, "E226", {"points": [v(1526.35, -935.44) * mm, v(1471.38, -835.94) * mm, v(1419.44, -734.8) * mm, v(1367.74, -633.58) * mm]});
            skFitSpline(sketch, "E227", {"points": [v(1367.74, -633.58) * mm, v(1552.73, -440.5) * mm, v(1742.3, -244.55) * mm, v(1859.63, -1.32) * mm]});
            skFitSpline(sketch, "E228", {"points": [v(1859.63, -1.32) * mm, v(2048.87, 252.77) * mm, v(2265.35, 489.45) * mm, v(2401.93, 778.72) * mm]});
            skFitSpline(sketch, "E229", {"points": [v(2401.93, 778.72) * mm, v(2672.61, 1271.3) * mm, v(2802.15, 1824.41) * mm, v(3020.74, 2338.03) * mm]});
            skFitSpline(sketch, "E230", {"points": [v(3020.74, 2338.03) * mm, v(3056.95, 2387.75) * mm, v(3051.2, 2454.97) * mm, v(3045.55, 2505.91) * mm]});
            skFitSpline(sketch, "E231", {"points": [v(3045.55, 2505.91) * mm, v(3679.45, 2889.08) * mm, v(3338.33, 2923.13) * mm, v(3748.66, 3116.26) * mm]});
            skFitSpline(sketch, "E232", {"points": [v(-235.44, 2352.25) * mm, v(-328.62, 2298.73) * mm, v(-285.67, 2159.14) * mm, v(-280.9, 2072.37) * mm]});
            skFitSpline(sketch, "E233", {"points": [v(-280.9, 2072.37) * mm, v(-284.79, 2012.34) * mm, v(-229.71, 1802.35) * mm, v(-288.7, 1942.85) * mm]});
            skFitSpline(sketch, "E234", {"points": [v(-288.7, 1942.85) * mm, v(-330.12, 2007.48) * mm, v(-357.84, 2079.38) * mm, v(-390.51, 2148.5) * mm]});
            skFitSpline(sketch, "E235", {"points": [v(-390.51, 2148.5) * mm, v(-426.79, 2034.24) * mm, v(-468.64, 1921) * mm, v(-421.17, 1804.04) * mm]});
            skFitSpline(sketch, "E236", {"points": [v(-421.17, 1804.04) * mm, v(-331.88, 1339.38) * mm, v(-349.35, 856.07) * mm, v(-223.05, 397.28) * mm]});
            skFitSpline(sketch, "E237", {"points": [v(-223.05, 397.28) * mm, v(-210.85, 321.76) * mm, v(-92.7, 321.43) * mm, v(-97.14, 404.98) * mm]});
            skFitSpline(sketch, "E238", {"points": [v(-97.14, 404.98) * mm, v(-91.83, 625.73) * mm, v(-155.12, 838.97) * mm, v(-160.2, 1058.51) * mm]});
            skFitSpline(sketch, "E239", {"points": [v(-160.2, 1058.51) * mm, v(-177.26, 1225.24) * mm, v(-163.06, 1125) * mm, v(-147.78, 1018.56) * mm]});
            skFitSpline(sketch, "E240", {"points": [v(-147.78, 1018.56) * mm, v(-156.14, 957.1) * mm, v(-99.39, 797.36) * mm, v(-15.8, 866.98) * mm]});
            skFitSpline(sketch, "E241", {"points": [v(-15.8, 866.98) * mm, v(53.95, 1001.33) * mm, v(-24.64, 1160.2) * mm, v(-21.82, 1301.32) * mm]});
            skFitSpline(sketch, "E242", {"points": [v(-21.82, 1301.32) * mm, v(-64.66, 1633.86) * mm, v(-92.5, 1972.08) * mm, v(-168.24, 2298) * mm]});
            skFitSpline(sketch, "E243", {"points": [v(-168.24, 2298) * mm, v(-180.88, 2324.14) * mm, v(-200.88, 2358.88) * mm, v(-235.44, 2352.25) * mm]});
            skFitSpline(sketch, "E244", {"points": [v(-3826.47, 2315.7) * mm, v(-3753.5, 2294.13) * mm, v(-3699.44, 2227.23) * mm, v(-3704.54, 2152.48) * mm]});
            skFitSpline(sketch, "E245", {"points": [v(-3704.54, 2152.48) * mm, v(-3498.36, 1648.51) * mm, v(-3320.24, 1106.7) * mm, v(-2934.63, 704.09) * mm]});
            skFitSpline(sketch, "E246", {"points": [v(-2934.63, 704.09) * mm, v(-2471.84, 154.57) * mm, v(-1906.72, -301.56) * mm, v(-1357.2, -754.69) * mm]});
            skFitSpline(sketch, "E247", {"points": [v(-1357.2, -754.69) * mm, v(-1477.2, -843.03) * mm, v(-1502.54, -1028.4) * mm, v(-1427.55, -1153.33) * mm]});
            skFitSpline(sketch, "E248", {"points": [v(-1427.55, -1153.33) * mm, v(-1511.96, -1099.51) * mm, v(-1579.44, -1187.12) * mm, v(-1638.29, -1231.39) * mm]});
            skFitSpline(sketch, "E249", {"points": [v(-1638.29, -1231.39) * mm, v(-1999.13, -1158.5) * mm, v(-2356.47, -1048.4) * mm, v(-2723.36, -993.34) * mm]});
            skFitSpline(sketch, "E250", {"points": [v(-2723.36, -993.34) * mm, v(-3094.9, -904.79) * mm, v(-3437.9, -730.45) * mm, v(-3775.8, -553.88) * mm]});
            skFitSpline(sketch, "E251", {"points": [v(-3775.8, -553.88) * mm, v(-4259.58, -214.95) * mm, v(-5022.2, 447) * mm, v(-4831.02, 1174.23) * mm]});
            skFitSpline(sketch, "E252", {"points": [v(-4831.02, 1174.23) * mm, v(-4732.68, 1266.58) * mm, v(-4689.61, 1016.57) * mm, v(-4565, 1199.13) * mm]});
            skFitSpline(sketch, "E253", {"points": [v(-4565, 1199.13) * mm, v(-4536.37, 1259.9) * mm, v(-4654.56, 1305.45) * mm, v(-4562.2, 1308.25) * mm]});
            skFitSpline(sketch, "E254", {"points": [v(-4562.2, 1308.25) * mm, v(-4510.21, 1338.03) * mm, v(-4682.6, 1405.93) * mm, v(-4655.1, 1493.47) * mm]});
            skFitSpline(sketch, "E255", {"points": [v(-4655.1, 1493.47) * mm, v(-4652.54, 1591.49) * mm, v(-4652.83, 1697.85) * mm, v(-4624.67, 1789.86) * mm]});
            skFitSpline(sketch, "E256", {"points": [v(-4624.67, 1789.86) * mm, v(-4592.73, 1818.59) * mm, v(-4467.94, 1845.82) * mm, v(-4531.58, 1786.33) * mm]});
            skFitSpline(sketch, "E257", {"points": [v(-4531.58, 1786.33) * mm, v(-4593, 1652.82) * mm, v(-4437.18, 1547.4) * mm, v(-4331.97, 1503.3) * mm]});
            skFitSpline(sketch, "E258", {"points": [v(-4331.97, 1503.3) * mm, v(-4279.42, 1472.02) * mm, v(-4317.4, 1583.87) * mm, v(-4325.27, 1623.14) * mm]});
            skFitSpline(sketch, "E259", {"points": [v(-4325.27, 1623.14) * mm, v(-4381.37, 1785.59) * mm, v(-4422.2, 2000.98) * mm, v(-4386.55, 1998.15) * mm]});
            skFitSpline(sketch, "E260", {"points": [v(-4386.55, 1998.15) * mm, v(-4127.71, 1931.6) * mm, v(-3987.82, 1543.06) * mm, v(-3782.75, 1426.39) * mm]});
            skFitSpline(sketch, "E261", {"points": [v(-3782.75, 1426.39) * mm, v(-3760.06, 1638) * mm, v(-3938.56, 1797.8) * mm, v(-3946.13, 2001.3) * mm]});
            skFitSpline(sketch, "E262", {"points": [v(-3946.13, 2001.3) * mm, v(-3905.3, 2147.63) * mm, v(-3924.57, 2245.06) * mm, v(-3826.47, 2315.7) * mm]});
            skFitSpline(sketch, "E263", {"points": [v(-5468.3, -83.03) * mm, v(-5580.77, -75.02) * mm, v(-5640.33, -258.28) * mm, v(-5521.4, -295.78) * mm]});
            skFitSpline(sketch, "E264", {"points": [v(-5521.4, -295.78) * mm, v(-5335.8, -343.5) * mm, v(-5300.29, -567.67) * mm, v(-5153.39, -667.7) * mm]});
            skFitSpline(sketch, "E265", {"points": [v(-5153.39, -667.7) * mm, v(-5141.88, -751.07) * mm, v(-5131.52, -853) * mm, v(-5077.34, -916.2) * mm]});
            skFitSpline(sketch, "E266", {"points": [v(-5077.34, -916.2) * mm, v(-5216.67, -974.77) * mm, v(-5403.84, -902.93) * mm, v(-5522.15, -1025.67) * mm]});
            skFitSpline(sketch, "E267", {"points": [v(-5522.15, -1025.67) * mm, v(-5584.17, -1067.63) * mm, v(-5555.54, -1128.43) * mm, v(-5498.67, -1161.14) * mm]});
            skFitSpline(sketch, "E268", {"points": [v(-5498.67, -1161.14) * mm, v(-5382.3, -1231.12) * mm, v(-5239.9, -1189.48) * mm, v(-5113.35, -1218.51) * mm]});
            skFitSpline(sketch, "E269", {"points": [v(-5113.35, -1218.51) * mm, v(-5061.95, -1220.73) * mm, v(-4965.37, -1180.63) * mm, v(-4995.6, -1273.28) * mm]});
            skFitSpline(sketch, "E270", {"points": [v(-4995.6, -1273.28) * mm, v(-4970.11, -1709.95) * mm, v(-4851.01, -2179.22) * mm, v(-4516.4, -2483.33) * mm]});
            skFitSpline(sketch, "E271", {"points": [v(-4516.4, -2483.33) * mm, v(-4460.98, -2527.77) * mm, v(-4378.13, -2541.35) * mm, v(-4341.5, -2606.33) * mm]});
            skFitSpline(sketch, "E272", {"points": [v(-4341.5, -2606.33) * mm, v(-4472.45, -2771.53) * mm, v(-4685.31, -2869.23) * mm, v(-4759.44, -3078.79) * mm]});
            skFitSpline(sketch, "E273", {"points": [v(-4759.44, -3078.79) * mm, v(-4831.42, -3234.1) * mm, v(-4848.78, -3416.42) * mm, v(-4794.34, -3579.93) * mm]});
            skFitSpline(sketch, "E274", {"points": [v(-4794.34, -3579.93) * mm, v(-4435.2, -3640.6) * mm, v(-4107.2, -3386.23) * mm, v(-3757.6, -3411.27) * mm]});
            skFitSpline(sketch, "E275", {"points": [v(-3757.6, -3411.27) * mm, v(-3489.29, -3487.21) * mm, v(-3206.43, -3478.62) * mm, v(-2933.58, -3521.44) * mm]});
            skFitSpline(sketch, "E276", {"points": [v(-2933.58, -3521.44) * mm, v(-2841.61, -3544.36) * mm, v(-2933.13, -3639.53) * mm, v(-2958.17, -3684.33) * mm]});
            skFitSpline(sketch, "E277", {"points": [v(-2958.17, -3684.33) * mm, v(-3066.14, -3815.53) * mm, v(-3137.67, -3994.57) * mm, v(-3071.58, -4161.77) * mm]});
            skFitSpline(sketch, "E278", {"points": [v(-3071.58, -4161.77) * mm, v(-3050.89, -4253.07) * mm, v(-2993.43, -4365.15) * mm, v(-2882.46, -4353.87) * mm]});
            skFitSpline(sketch, "E279", {"points": [v(-2882.46, -4353.87) * mm, v(-2433.18, -4242.56) * mm, v(-1971.74, -4164.86) * mm, v(-1528.3, -4027.5) * mm]});
            skFitSpline(sketch, "E280", {"points": [v(-1528.3, -4027.5) * mm, v(-1336.5, -4029.67) * mm, v(-1114.1, -4069.15) * mm, v(-959.67, -3922.98) * mm]});
            skFitSpline(sketch, "E281", {"points": [v(-959.67, -3922.98) * mm, v(-877.85, -3880.38) * mm, v(-785.84, -3826.38) * mm, v(-722.25, -3769.43) * mm]});
            skFitSpline(sketch, "E282", {"points": [v(-722.25, -3769.43) * mm, v(-630.73, -3776.61) * mm, v(-550.17, -3692) * mm, v(-462.62, -3683.96) * mm]});
            skFitSpline(sketch, "E283", {"points": [v(-462.62, -3683.96) * mm, v(-348.19, -3652.67) * mm, v(-220.71, -3641.05) * mm, v(-108.9, -3684.08) * mm]});
            skFitSpline(sketch, "E284", {"points": [v(-108.9, -3684.08) * mm, v(-100.71, -3827.85) * mm, v(-119.6, -3972.34) * mm, v(-103.9, -4115.72) * mm]});
            skFitSpline(sketch, "E285", {"points": [v(-103.9, -4115.72) * mm, v(-109.02, -4201.57) * mm, v(-145.1, -4354.7) * mm, v(-30.35, -4383.16) * mm]});
            skFitSpline(sketch, "E286", {"points": [v(-30.35, -4383.16) * mm, v(156.75, -4386.9) * mm, v(371.27, -4395.57) * mm, v(519.6, -4270.2) * mm]});
            skFitSpline(sketch, "E287", {"points": [v(519.6, -4270.2) * mm, v(688.96, -4337.81) * mm, v(863.32, -4232.73) * mm, v(1014.35, -4162.63) * mm]});
            skFitSpline(sketch, "E288", {"points": [v(1014.35, -4162.63) * mm, v(1147.16, -4116.76) * mm, v(1106.7, -3964.28) * mm, v(1100.63, -3858.06) * mm]});
            skFitSpline(sketch, "E289", {"points": [v(1100.63, -3858.06) * mm, v(1130.99, -3664.58) * mm, v(1355.52, -3602.78) * mm, v(1519.92, -3565.6) * mm]});
            skFitSpline(sketch, "E290", {"points": [v(1519.92, -3565.6) * mm, v(1614.87, -3542.39) * mm, v(1648.13, -3525.49) * mm, v(1743.8, -3528.4) * mm]});
            skFitSpline(sketch, "E291", {"points": [v(1743.8, -3528.4) * mm, v(1968, -3509.5) * mm, v(2251.79, -3504.13) * mm, v(2469.64, -3448.83) * mm]});
            skFitSpline(sketch, "E292", {"points": [v(2469.64, -3448.83) * mm, v(2618.4, -3082.13) * mm, v(1680.97, -3376.54) * mm, v(1521.1, -3491.83) * mm]});
            skFitSpline(sketch, "E293", {"points": [v(1521.1, -3491.83) * mm, v(1470.58, -3481.67) * mm, v(1437.08, -3441.92) * mm, v(1502.17, -3433.15) * mm]});
            skFitSpline(sketch, "E294", {"points": [v(1502.17, -3433.15) * mm, v(1604.6, -3382.96) * mm, v(1574.66, -3199.11) * mm, v(1450.12, -3212.07) * mm]});
            skFitSpline(sketch, "E295", {"points": [v(1450.12, -3212.07) * mm, v(1386.65, -3208.07) * mm, v(1324.06, -3196.03) * mm, v(1261, -3188.4) * mm]});
            skFitSpline(sketch, "E296", {"points": [v(1261, -3188.4) * mm, v(1307.46, -3351.82) * mm, v(1130.45, -3421.03) * mm, v(1064.2, -3541.5) * mm]});
            skFitSpline(sketch, "E297", {"points": [v(1064.2, -3541.5) * mm, v(987.78, -3637.65) * mm, v(966.34, -3798.5) * mm, v(922.82, -3879.41) * mm]});
            skFitSpline(sketch, "E298", {"points": [v(922.82, -3879.41) * mm, v(918.99, -3813.14) * mm, v(822.43, -3777.27) * mm, v(814.7, -3860.14) * mm]});
            skFitSpline(sketch, "E299", {"points": [v(814.7, -3860.14) * mm, v(835.15, -3945.26) * mm, v(750.55, -3992.76) * mm, v(676.25, -3984.45) * mm]});
            skFitSpline(sketch, "E300", {"points": [v(676.25, -3984.45) * mm, v(594.54, -3985.15) * mm, v(509.54, -4036.3) * mm, v(504.05, -4124.76) * mm]});
            skFitSpline(sketch, "E301", {"points": [v(504.05, -4124.76) * mm, v(522.92, -4150.64) * mm, v(609.23, -4155.24) * mm, v(598.67, -4158.35) * mm]});
            skFitSpline(sketch, "E302", {"points": [v(598.67, -4158.35) * mm, v(561.43, -4178.35) * mm, v(494.18, -4191.14) * mm, v(500.97, -4244.12) * mm]});
            skFitSpline(sketch, "E303", {"points": [v(500.97, -4244.12) * mm, v(365.76, -4154.08) * mm, v(206.95, -4256.35) * mm, v(65.3, -4212.34) * mm]});
            skFitSpline(sketch, "E304", {"points": [v(65.3, -4212.34) * mm, v(25.52, -4023.82) * mm, v(83.32, -3837.46) * mm, v(88.2, -3648.92) * mm]});
            skFitSpline(sketch, "E305", {"points": [v(88.2, -3648.92) * mm, v(87.2, -3549.72) * mm, v(-8.97, -3502.95) * mm, v(-95.13, -3495.14) * mm]});
            skFitSpline(sketch, "E306", {"points": [v(-95.13, -3495.14) * mm, v(-191, -3469.15) * mm, v(-290.56, -3451.46) * mm, v(-387.24, -3434.68) * mm]});
            skFitSpline(sketch, "E307", {"points": [v(-387.24, -3434.68) * mm, v(-195.27, -3412.22) * mm, v(27.31, -3423.63) * mm, v(172.61, -3270.52) * mm]});
            skFitSpline(sketch, "E308", {"points": [v(172.61, -3270.52) * mm, v(226.23, -3246.05) * mm, v(241.96, -3149.93) * mm, v(164.4, -3156.85) * mm]});
            skFitSpline(sketch, "E309", {"points": [v(164.4, -3156.85) * mm, v(-26, -3330.69) * mm, v(-812.19, -3187.99) * mm, v(-700.41, -3120.73) * mm]});
            skFitSpline(sketch, "E310", {"points": [v(-700.41, -3120.73) * mm, v(-604.22, -3028.73) * mm, v(-535.77, -2884.5) * mm, v(-408.37, -2837.36) * mm]});
            skFitSpline(sketch, "E311", {"points": [v(-408.37, -2837.36) * mm, v(-325.85, -2906.44) * mm, v(-486.45, -3039.35) * mm, v(-374, -3091.74) * mm]});
            skFitSpline(sketch, "E312", {"points": [v(-374, -3091.74) * mm, v(-245.38, -3086.22) * mm, v(-220.51, -2918.01) * mm, v(-156.4, -2835.98) * mm]});
            skFitSpline(sketch, "E313", {"points": [v(-156.4, -2835.98) * mm, v(-135.07, -2781.17) * mm, v(-104.34, -2780.25) * mm, v(-60.67, -2799.52) * mm]});
            skFitSpline(sketch, "E314", {"points": [v(-60.67, -2799.52) * mm, v(33.9, -2815.2) * mm, v(134.03, -2678.58) * mm, v(38.48, -2615.45) * mm]});
            skFitSpline(sketch, "E315", {"points": [v(38.48, -2615.45) * mm, v(-175.31, -2525.86) * mm, v(-417.1, -2627.47) * mm, v(-606.02, -2734.07) * mm]});
            skFitSpline(sketch, "E316", {"points": [v(-606.02, -2734.07) * mm, v(-763.7, -2836.19) * mm, v(-923.36, -2959.3) * mm, v(-1024.37, -3116.4) * mm]});
            skFitSpline(sketch, "E317", {"points": [v(-1024.37, -3116.4) * mm, v(-1168.11, -3328.73) * mm, v(-1085.85, -3344.83) * mm, v(-1021.36, -3403.35) * mm]});
            skFitSpline(sketch, "E318", {"points": [v(-1021.36, -3403.35) * mm, v(-934.28, -3484.07) * mm, v(-817.43, -3508.51) * mm, v(-708.56, -3537.1) * mm]});
            skFitSpline(sketch, "E319", {"points": [v(-708.56, -3537.1) * mm, v(-667.46, -3541.87) * mm, v(-569.24, -3547.41) * mm, v(-659.52, -3582.87) * mm]});
            skFitSpline(sketch, "E320", {"points": [v(-659.52, -3582.87) * mm, v(-707.16, -3600.82) * mm, v(-751.31, -3640.8) * mm, v(-769.43, -3681.96) * mm]});
            skFitSpline(sketch, "E321", {"points": [v(-769.43, -3681.96) * mm, v(-1203.23, -3711.6) * mm, v(-1642.07, -3704.46) * mm, v(-2070.08, -3781.08) * mm]});
            skFitSpline(sketch, "E322", {"points": [v(-2070.08, -3781.08) * mm, v(-2181.74, -3771.88) * mm, v(-2270.06, -3839.91) * mm, v(-2365.61, -3881.6) * mm]});
            skFitSpline(sketch, "E323", {"points": [v(-2365.61, -3881.6) * mm, v(-3310.63, -4345.19) * mm, v(-2387.86, -3383.24) * mm, v(-2310.55, -3328.6) * mm]});
            skFitSpline(sketch, "E324", {"points": [v(-2310.55, -3328.6) * mm, v(-2236.74, -3300.6) * mm, v(-2285.1, -3394.2) * mm, v(-2229.5, -3411.54) * mm]});
            skFitSpline(sketch, "E325", {"points": [v(-2229.5, -3411.54) * mm, v(-2094.62, -3466.3) * mm, v(-1973.26, -3341.6) * mm, v(-1837.53, -3360.38) * mm]});
            skFitSpline(sketch, "E326", {"points": [v(-1837.53, -3360.38) * mm, v(-1506.65, -3326.58) * mm, v(-1197.83, -3179.94) * mm, v(-938.43, -2980.3) * mm]});
            skFitSpline(sketch, "E327", {"points": [v(-938.43, -2980.3) * mm, v(-820.85, -2884.02) * mm, v(-714.9, -2767.89) * mm, v(-660.38, -2623.08) * mm]});
            skFitSpline(sketch, "E328", {"points": [v(-660.38, -2623.08) * mm, v(-1204.28, -2626.13) * mm, v(-901.36, -2712.16) * mm, v(-1137.45, -2928.89) * mm]});
            skFitSpline(sketch, "E329", {"points": [v(-1137.45, -2928.89) * mm, v(-1112.12, -2870.36) * mm, v(-1170.16, -2771.07) * mm, v(-1231.4, -2832.9) * mm]});
            skFitSpline(sketch, "E330", {"points": [v(-1231.4, -2832.9) * mm, v(-1306.88, -2933.31) * mm, v(-1351.1, -3073.3) * mm, v(-1493.37, -3101.08) * mm]});
            skFitSpline(sketch, "E331", {"points": [v(-1493.37, -3101.08) * mm, v(-1939.34, -3211.14) * mm, v(-2403.5, -3068.48) * mm, v(-2852.95, -3164.96) * mm]});
            skFitSpline(sketch, "E332", {"points": [v(-2852.95, -3164.96) * mm, v(-3889.93, -3138.51) * mm, v(-4326.58, -3357.12) * mm, v(-4609.08, -3398.36) * mm]});
            skFitSpline(sketch, "E333", {"points": [v(-4609.08, -3398.36) * mm, v(-4651.14, -3178.24) * mm, v(-4506.2, -2970.6) * mm, v(-4326.65, -2856.7) * mm]});
            skFitSpline(sketch, "E334", {"points": [v(-4326.65, -2856.7) * mm, v(-4228.07, -2718.62) * mm, v(-4101.01, -2732.75) * mm, v(-4082.5, -2617.69) * mm]});
            skFitSpline(sketch, "E335", {"points": [v(-4082.5, -2617.69) * mm, v(-4084.3, -2474.77) * mm, v(-4262.67, -2445.38) * mm, v(-4348.7, -2367.03) * mm]});
            skFitSpline(sketch, "E336", {"points": [v(-4348.7, -2367.03) * mm, v(-5069.37, -1233.86) * mm, v(-4439.98, -1220.57) * mm, v(-4922.74, -736.95) * mm]});
            skFitSpline(sketch, "E337", {"points": [v(-4922.74, -736.95) * mm, v(-4935.2, -691.3) * mm, v(-4847.62, -719.3) * mm, v(-4832.1, -670.72) * mm]});
            skFitSpline(sketch, "E338", {"points": [v(-4832.1, -670.72) * mm, v(-4777.13, -591.38) * mm, v(-4909.01, -497.51) * mm, v(-4979.26, -538.26) * mm]});
            skFitSpline(sketch, "E339", {"points": [v(-4979.26, -538.26) * mm, v(-5021.78, -573.4) * mm, v(-5064.9, -469.76) * mm, v(-5097.65, -443.57) * mm]});
            skFitSpline(sketch, "E340", {"points": [v(-5097.65, -443.57) * mm, v(-5109.72, -425.54) * mm, v(-5165.39, -345.28) * mm, v(-5117.33, -395.38) * mm]});
            skFitSpline(sketch, "E341", {"points": [v(-5117.33, -395.38) * mm, v(-5070, -439.4) * mm, v(-4998.2, -430.59) * mm, v(-4960.99, -387.6) * mm]});
            skFitSpline(sketch, "E342", {"points": [v(-4960.99, -387.6) * mm, v(-4878.9, -394.89) * mm, v(-4747.38, -470.62) * mm, v(-4693.4, -368.52) * mm]});
            skFitSpline(sketch, "E343", {"points": [v(-4693.4, -368.52) * mm, v(-4674.9, -260.17) * mm, v(-4829.74, -260.62) * mm, v(-4894.13, -224.74) * mm]});
            skFitSpline(sketch, "E344", {"points": [v(-4894.13, -224.74) * mm, v(-5079.66, -158.04) * mm, v(-5269.45, -91.6) * mm, v(-5468.3, -83.03) * mm]});
            skFitSpline(sketch, "E345", {"points": [v(4222.52, -566.6) * mm, v(4388.94, -1421.17) * mm, v(3949.18, -1994.58) * mm, v(3683.84, -2248) * mm]});
            skFitSpline(sketch, "E346", {"points": [v(3683.84, -2248) * mm, v(3441.1, -2206.05) * mm, v(3187.6, -2302.56) * mm, v(2953.86, -2205.31) * mm]});
            skFitSpline(sketch, "E347", {"points": [v(2953.86, -2205.31) * mm, v(2483.8, -2169.89) * mm, v(1993.29, -2263.41) * mm, v(1547.93, -2069.47) * mm]});
            skFitSpline(sketch, "E348", {"points": [v(1547.93, -2069.47) * mm, v(1459.6, -2037.98) * mm, v(1331.04, -1955.5) * mm, v(1260.96, -1965.18) * mm]});
            skFitSpline(sketch, "E349", {"points": [v(1260.96, -1965.18) * mm, v(1312.64, -1903.1) * mm, v(1346.73, -1804.1) * mm, v(1298.24, -1731.23) * mm]});
            skFitSpline(sketch, "E350", {"points": [v(1298.24, -1731.23) * mm, v(1642.98, -1682.87) * mm, v(1992.2, -1594.8) * mm, v(2293.34, -1416.16) * mm]});
            skFitSpline(sketch, "E351", {"points": [v(2293.34, -1416.16) * mm, v(2342.51, -1384.96) * mm, v(2358.7, -1323.88) * mm, v(2334.79, -1276.74) * mm]});
            skFitSpline(sketch, "E352", {"points": [v(2334.79, -1276.74) * mm, v(2790.4, -977.53) * mm, v(3143.57, -899.34) * mm, v(3557.67, -681.24) * mm]});
            skFitSpline(sketch, "E353", {"points": [v(3557.67, -681.24) * mm, v(3873.91, -554.42) * mm, v(4086.09, -393.59) * mm, v(4222.52, -566.6) * mm]});
            skLineSegment(sketch, "E354", {"start": v(-5468.3, -83.03) * mm, "end": v(-5468.3, -83.03) * mm});
            skFitSpline(sketch, "E355", {"points": [v(-2692.59, -2237.72) * mm, v(-2775.04, -2258.8) * mm, v(-2722.46, -2354.32) * mm, v(-2662.71, -2366.6) * mm]});
            skFitSpline(sketch, "E356", {"points": [v(-2662.71, -2366.6) * mm, v(-2650.42, -2379.82) * mm, v(-2551.56, -2398.72) * mm, v(-2619.1, -2392.28) * mm]});
            skFitSpline(sketch, "E357", {"points": [v(-2619.1, -2392.28) * mm, v(-2672.95, -2403.39) * mm, v(-2864.87, -2361.31) * mm, v(-2808.06, -2416.1) * mm]});
            skFitSpline(sketch, "E358", {"points": [v(-2808.06, -2416.1) * mm, v(-2736.87, -2496.8) * mm, v(-2645.9, -2574.69) * mm, v(-2530.89, -2549.85) * mm]});
            skFitSpline(sketch, "E359", {"points": [v(-2530.89, -2549.85) * mm, v(-2451.2, -2541.68) * mm, v(-2376.35, -2507.96) * mm, v(-2297.52, -2527.64) * mm]});
            skFitSpline(sketch, "E360", {"points": [v(-2297.52, -2527.64) * mm, v(-2194.58, -2513.16) * mm, v(-2092.62, -2493.47) * mm, v(-1990.68, -2465.47) * mm]});
            skFitSpline(sketch, "E361", {"points": [v(-1990.68, -2465.47) * mm, v(-2081.28, -2518.07) * mm, v(-2213.42, -2522.56) * mm, v(-2277.88, -2609.83) * mm]});
            skFitSpline(sketch, "E362", {"points": [v(-2277.88, -2609.83) * mm, v(-2281.34, -2706.71) * mm, v(-2139.78, -2687.08) * mm, v(-2076.51, -2672.64) * mm]});
            skFitSpline(sketch, "E363", {"points": [v(-2076.51, -2672.64) * mm, v(-1783.9, -2604.15) * mm, v(-1516.4, -2452.69) * mm, v(-1218, -2405.38) * mm]});
            skFitSpline(sketch, "E364", {"points": [v(-1218, -2405.38) * mm, v(-1118.87, -2374.21) * mm, v(-1036.83, -2307.3) * mm, v(-960.71, -2239.03) * mm]});
            skFitSpline(sketch, "E365", {"points": [v(-960.71, -2239.03) * mm, v(-1046.5, -2203.65) * mm, v(-1167.85, -2199.43) * mm, v(-1243.86, -2212.57) * mm]});
            skFitSpline(sketch, "E366", {"points": [v(-1243.86, -2212.57) * mm, v(-1210.94, -2165.57) * mm, v(-1122.39, -2077.4) * mm, v(-1194.15, -2030.67) * mm]});
            skFitSpline(sketch, "E367", {"points": [v(-1194.15, -2030.67) * mm, v(-1957.69, -2096.51) * mm, v(-1762.4, -2234.2) * mm, v(-2692.59, -2237.72) * mm]});
            skSolve(sketch);
        }
        {
            var Q0;
            Q0=qCreatedBy(makeId("Top.planeOp"),FACE);
            var sketch = newSketch(context, id + "F1", { "sketchPlane" : qUnion([Q0])});
            skLineSegment(sketch, "E368.bottom", {"start": v(6013.3, -4852.85) * mm, "end": v(-6013.3, -4852.85) * mm});
            skLineSegment(sketch, "E368.top", {"start": v(6013.3, 4852.85) * mm, "end": v(-6013.3, 4852.85) * mm});
            skLineSegment(sketch, "E368.left", {"start": v(6013.3, -4852.85) * mm, "end": v(6013.3, 4852.85) * mm});
            skLineSegment(sketch, "E368.right", {"start": v(-6013.3, -4852.85) * mm, "end": v(-6013.3, 4852.85) * mm});
            skPoint(sketch, "E368.middle", {"position": v(0, 0) * mm});
            skSolve(sketch);
        }
        {
            var Q0;
            Q0 = qSketchRegion(id + "F1", true);
            extrude(context, id + "F2", {"entities" : qUnion([Q0]), "oppositeDirection" : true, "depth" : 500 * mm});
        }
        {
            var Q0;
            Q0=makeQuery(id+"F0.imprint","IMPRINT",FACE,{"disambiguationData":[TD([[makeQuery(id+"F0.imprint","IMPRINT",EDGE,{"derivedFrom":sQuery(id+"F0.wireOp",EDGE,"E263")}),1.0]])]});
            var Q1;
            Q1=makeQuery(id+"F0.imprint","IMPRINT",FACE,{"disambiguationData":[TD([[makeQuery(id+"F0.imprint","IMPRINT",EDGE,{"derivedFrom":sQuery(id+"F0.wireOp",EDGE,"E355")}),1.0]])]});
            var Q2;
            Q2=makeQuery(id+"F0.imprint","IMPRINT",FACE,{"disambiguationData":[TD([[makeQuery(id+"F0.imprint","IMPRINT",EDGE,{"derivedFrom":sQuery(id+"F0.wireOp",EDGE,"E0")}),1.0]])]});
            var Q3;
            Q3=makeQuery(id+"F0.imprint","IMPRINT",FACE,{"disambiguationData":[TD([[makeQuery(id+"F0.imprint","IMPRINT",EDGE,{"derivedFrom":sQuery(id+"F0.wireOp",EDGE,"E232")}),1.0]])]});
            extrude(context, id + "F3", {"entities" : qUnion([Q0, Q1, Q2, Q3]), "depth" : 1000 * mm});
        }
        {
            var Q0;
            Q0=makeQuery(id+"F2.opExtrude","SWEPT_BODY",BODY,{"disambiguationData":[OSD([sQuery(id+"F1.wireOp",EDGE,"E368.bottom"),sQuery(id+"F1.wireOp",EDGE,"E368.top"),sQuery(id+"F1.wireOp",EDGE,"E368.left"),sQuery(id+"F1.wireOp",EDGE,"E368.right")])]});
            var Q1;
            Q1=makeQuery(id+"F3.opExtrude","SWEPT_BODY",BODY,{"disambiguationData":[OSD([sQuery(id+"F0.wireOp",EDGE,"E355"),sQuery(id+"F0.wireOp",EDGE,"E356"),sQuery(id+"F0.wireOp",EDGE,"E357"),sQuery(id+"F0.wireOp",EDGE,"E358"),sQuery(id+"F0.wireOp",EDGE,"E359"),sQuery(id+"F0.wireOp",EDGE,"E360"),sQuery(id+"F0.wireOp",EDGE,"E361"),sQuery(id+"F0.wireOp",EDGE,"E362"),sQuery(id+"F0.wireOp",EDGE,"E363"),sQuery(id+"F0.wireOp",EDGE,"E364"),sQuery(id+"F0.wireOp",EDGE,"E365"),sQuery(id+"F0.wireOp",EDGE,"E366"),sQuery(id+"F0.wireOp",EDGE,"E367")])]});
            var Q2;
            Q2=makeQuery(id+"F3.opExtrude","SWEPT_BODY",BODY,{"disambiguationData":[OSD([sQuery(id+"F0.wireOp",EDGE,"E232"),sQuery(id+"F0.wireOp",EDGE,"E233"),sQuery(id+"F0.wireOp",EDGE,"E234"),sQuery(id+"F0.wireOp",EDGE,"E235"),sQuery(id+"F0.wireOp",EDGE,"E236"),sQuery(id+"F0.wireOp",EDGE,"E237"),sQuery(id+"F0.wireOp",EDGE,"E238"),sQuery(id+"F0.wireOp",EDGE,"E239"),sQuery(id+"F0.wireOp",EDGE,"E240"),sQuery(id+"F0.wireOp",EDGE,"E241"),sQuery(id+"F0.wireOp",EDGE,"E242"),sQuery(id+"F0.wireOp",EDGE,"E243")])]});
            var Q3;
            Q3=makeQuery(id+"F3.opExtrude","SWEPT_BODY",BODY,{"disambiguationData":[OSD([sQuery(id+"F0.wireOp",EDGE,"E111"),sQuery(id+"F0.wireOp",EDGE,"E263"),sQuery(id+"F0.wireOp",EDGE,"E264"),sQuery(id+"F0.wireOp",EDGE,"E265"),sQuery(id+"F0.wireOp",EDGE,"E266"),sQuery(id+"F0.wireOp",EDGE,"E267"),sQuery(id+"F0.wireOp",EDGE,"E268"),sQuery(id+"F0.wireOp",EDGE,"E269"),sQuery(id+"F0.wireOp",EDGE,"E270"),sQuery(id+"F0.wireOp",EDGE,"E271"),sQuery(id+"F0.wireOp",EDGE,"E272"),sQuery(id+"F0.wireOp",EDGE,"E273"),sQuery(id+"F0.wireOp",EDGE,"E274"),sQuery(id+"F0.wireOp",EDGE,"E275"),sQuery(id+"F0.wireOp",EDGE,"E276"),sQuery(id+"F0.wireOp",EDGE,"E277"),sQuery(id+"F0.wireOp",EDGE,"E278"),sQuery(id+"F0.wireOp",EDGE,"E279"),sQuery(id+"F0.wireOp",EDGE,"E280"),sQuery(id+"F0.wireOp",EDGE,"E281"),sQuery(id+"F0.wireOp",EDGE,"E282"),sQuery(id+"F0.wireOp",EDGE,"E283"),sQuery(id+"F0.wireOp",EDGE,"E284"),sQuery(id+"F0.wireOp",EDGE,"E285"),sQuery(id+"F0.wireOp",EDGE,"E286"),sQuery(id+"F0.wireOp",EDGE,"E287"),sQuery(id+"F0.wireOp",EDGE,"E288"),sQuery(id+"F0.wireOp",EDGE,"E289"),sQuery(id+"F0.wireOp",EDGE,"E290"),sQuery(id+"F0.wireOp",EDGE,"E291"),sQuery(id+"F0.wireOp",EDGE,"E292"),sQuery(id+"F0.wireOp",EDGE,"E293"),sQuery(id+"F0.wireOp",EDGE,"E294"),sQuery(id+"F0.wireOp",EDGE,"E295"),sQuery(id+"F0.wireOp",EDGE,"E296"),sQuery(id+"F0.wireOp",EDGE,"E297"),sQuery(id+"F0.wireOp",EDGE,"E298"),sQuery(id+"F0.wireOp",EDGE,"E299"),sQuery(id+"F0.wireOp",EDGE,"E300"),sQuery(id+"F0.wireOp",EDGE,"E301"),sQuery(id+"F0.wireOp",EDGE,"E302"),sQuery(id+"F0.wireOp",EDGE,"E303"),sQuery(id+"F0.wireOp",EDGE,"E304"),sQuery(id+"F0.wireOp",EDGE,"E305"),sQuery(id+"F0.wireOp",EDGE,"E306"),sQuery(id+"F0.wireOp",EDGE,"E307"),sQuery(id+"F0.wireOp",EDGE,"E308"),sQuery(id+"F0.wireOp",EDGE,"E309"),sQuery(id+"F0.wireOp",EDGE,"E310"),sQuery(id+"F0.wireOp",EDGE,"E311"),sQuery(id+"F0.wireOp",EDGE,"E312"),sQuery(id+"F0.wireOp",EDGE,"E313"),sQuery(id+"F0.wireOp",EDGE,"E314"),sQuery(id+"F0.wireOp",EDGE,"E315"),sQuery(id+"F0.wireOp",EDGE,"E316"),sQuery(id+"F0.wireOp",EDGE,"E317"),sQuery(id+"F0.wireOp",EDGE,"E318"),sQuery(id+"F0.wireOp",EDGE,"E319"),sQuery(id+"F0.wireOp",EDGE,"E320"),sQuery(id+"F0.wireOp",EDGE,"E321"),sQuery(id+"F0.wireOp",EDGE,"E322"),sQuery(id+"F0.wireOp",EDGE,"E323"),sQuery(id+"F0.wireOp",EDGE,"E324"),sQuery(id+"F0.wireOp",EDGE,"E325"),sQuery(id+"F0.wireOp",EDGE,"E326"),sQuery(id+"F0.wireOp",EDGE,"E327"),sQuery(id+"F0.wireOp",EDGE,"E328"),sQuery(id+"F0.wireOp",EDGE,"E329"),sQuery(id+"F0.wireOp",EDGE,"E330"),sQuery(id+"F0.wireOp",EDGE,"E331"),sQuery(id+"F0.wireOp",EDGE,"E332"),sQuery(id+"F0.wireOp",EDGE,"E333"),sQuery(id+"F0.wireOp",EDGE,"E334"),sQuery(id+"F0.wireOp",EDGE,"E335"),sQuery(id+"F0.wireOp",EDGE,"E336"),sQuery(id+"F0.wireOp",EDGE,"E337"),sQuery(id+"F0.wireOp",EDGE,"E338"),sQuery(id+"F0.wireOp",EDGE,"E339"),sQuery(id+"F0.wireOp",EDGE,"E340"),sQuery(id+"F0.wireOp",EDGE,"E341"),sQuery(id+"F0.wireOp",EDGE,"E342"),sQuery(id+"F0.wireOp",EDGE,"E343"),sQuery(id+"F0.wireOp",EDGE,"E344"),sQuery(id+"F0.wireOp",EDGE,"E354")])]});
            var Q4;
            Q4=makeQuery(id+"F3.opExtrude","SWEPT_BODY",BODY,{"disambiguationData":[OSD([sQuery(id+"F0.wireOp",EDGE,"E0"),sQuery(id+"F0.wireOp",EDGE,"E1"),sQuery(id+"F0.wireOp",EDGE,"E2"),sQuery(id+"F0.wireOp",EDGE,"E3"),sQuery(id+"F0.wireOp",EDGE,"E4"),sQuery(id+"F0.wireOp",EDGE,"E5"),sQuery(id+"F0.wireOp",EDGE,"E6"),sQuery(id+"F0.wireOp",EDGE,"E7"),sQuery(id+"F0.wireOp",EDGE,"E8"),sQuery(id+"F0.wireOp",EDGE,"E9"),sQuery(id+"F0.wireOp",EDGE,"E10"),sQuery(id+"F0.wireOp",EDGE,"E11"),sQuery(id+"F0.wireOp",EDGE,"E12"),sQuery(id+"F0.wireOp",EDGE,"E13"),sQuery(id+"F0.wireOp",EDGE,"E14"),sQuery(id+"F0.wireOp",EDGE,"E15"),sQuery(id+"F0.wireOp",EDGE,"E16"),sQuery(id+"F0.wireOp",EDGE,"E17"),sQuery(id+"F0.wireOp",EDGE,"E18"),sQuery(id+"F0.wireOp",EDGE,"E19"),sQuery(id+"F0.wireOp",EDGE,"E20"),sQuery(id+"F0.wireOp",EDGE,"E21"),sQuery(id+"F0.wireOp",EDGE,"E22"),sQuery(id+"F0.wireOp",EDGE,"E23"),sQuery(id+"F0.wireOp",EDGE,"E24"),sQuery(id+"F0.wireOp",EDGE,"E25"),sQuery(id+"F0.wireOp",EDGE,"E26"),sQuery(id+"F0.wireOp",EDGE,"E27"),sQuery(id+"F0.wireOp",EDGE,"E28"),sQuery(id+"F0.wireOp",EDGE,"E29"),sQuery(id+"F0.wireOp",EDGE,"E30"),sQuery(id+"F0.wireOp",EDGE,"E31"),sQuery(id+"F0.wireOp",EDGE,"E32"),sQuery(id+"F0.wireOp",EDGE,"E33"),sQuery(id+"F0.wireOp",EDGE,"E34"),sQuery(id+"F0.wireOp",EDGE,"E35"),sQuery(id+"F0.wireOp",EDGE,"E36"),sQuery(id+"F0.wireOp",EDGE,"E37"),sQuery(id+"F0.wireOp",EDGE,"E38"),sQuery(id+"F0.wireOp",EDGE,"E39"),sQuery(id+"F0.wireOp",EDGE,"E40"),sQuery(id+"F0.wireOp",EDGE,"E41"),sQuery(id+"F0.wireOp",EDGE,"E42"),sQuery(id+"F0.wireOp",EDGE,"E43"),sQuery(id+"F0.wireOp",EDGE,"E44"),sQuery(id+"F0.wireOp",EDGE,"E45"),sQuery(id+"F0.wireOp",EDGE,"E46"),sQuery(id+"F0.wireOp",EDGE,"E47"),sQuery(id+"F0.wireOp",EDGE,"E48"),sQuery(id+"F0.wireOp",EDGE,"E49"),sQuery(id+"F0.wireOp",EDGE,"E50"),sQuery(id+"F0.wireOp",EDGE,"E51"),sQuery(id+"F0.wireOp",EDGE,"E52"),sQuery(id+"F0.wireOp",EDGE,"E53"),sQuery(id+"F0.wireOp",EDGE,"E54"),sQuery(id+"F0.wireOp",EDGE,"E55"),sQuery(id+"F0.wireOp",EDGE,"E56"),sQuery(id+"F0.wireOp",EDGE,"E57"),sQuery(id+"F0.wireOp",EDGE,"E58"),sQuery(id+"F0.wireOp",EDGE,"E59"),sQuery(id+"F0.wireOp",EDGE,"E60"),sQuery(id+"F0.wireOp",EDGE,"E61"),sQuery(id+"F0.wireOp",EDGE,"E62"),sQuery(id+"F0.wireOp",EDGE,"E63"),sQuery(id+"F0.wireOp",EDGE,"E64"),sQuery(id+"F0.wireOp",EDGE,"E65"),sQuery(id+"F0.wireOp",EDGE,"E66"),sQuery(id+"F0.wireOp",EDGE,"E67"),sQuery(id+"F0.wireOp",EDGE,"E68"),sQuery(id+"F0.wireOp",EDGE,"E69"),sQuery(id+"F0.wireOp",EDGE,"E70"),sQuery(id+"F0.wireOp",EDGE,"E71"),sQuery(id+"F0.wireOp",EDGE,"E72"),sQuery(id+"F0.wireOp",EDGE,"E73"),sQuery(id+"F0.wireOp",EDGE,"E74"),sQuery(id+"F0.wireOp",EDGE,"E75"),sQuery(id+"F0.wireOp",EDGE,"E76"),sQuery(id+"F0.wireOp",EDGE,"E77"),sQuery(id+"F0.wireOp",EDGE,"E78"),sQuery(id+"F0.wireOp",EDGE,"E79"),sQuery(id+"F0.wireOp",EDGE,"E80"),sQuery(id+"F0.wireOp",EDGE,"E81"),sQuery(id+"F0.wireOp",EDGE,"E82"),sQuery(id+"F0.wireOp",EDGE,"E83"),sQuery(id+"F0.wireOp",EDGE,"E84"),sQuery(id+"F0.wireOp",EDGE,"E85"),sQuery(id+"F0.wireOp",EDGE,"E86"),sQuery(id+"F0.wireOp",EDGE,"E87"),sQuery(id+"F0.wireOp",EDGE,"E88"),sQuery(id+"F0.wireOp",EDGE,"E89"),sQuery(id+"F0.wireOp",EDGE,"E90"),sQuery(id+"F0.wireOp",EDGE,"E91"),sQuery(id+"F0.wireOp",EDGE,"E92"),sQuery(id+"F0.wireOp",EDGE,"E93"),sQuery(id+"F0.wireOp",EDGE,"E94"),sQuery(id+"F0.wireOp",EDGE,"E95"),sQuery(id+"F0.wireOp",EDGE,"E96"),sQuery(id+"F0.wireOp",EDGE,"E97"),sQuery(id+"F0.wireOp",EDGE,"E98"),sQuery(id+"F0.wireOp",EDGE,"E99"),sQuery(id+"F0.wireOp",EDGE,"E100"),sQuery(id+"F0.wireOp",EDGE,"E101"),sQuery(id+"F0.wireOp",EDGE,"E102"),sQuery(id+"F0.wireOp",EDGE,"E103"),sQuery(id+"F0.wireOp",EDGE,"E104"),sQuery(id+"F0.wireOp",EDGE,"E105"),sQuery(id+"F0.wireOp",EDGE,"E106"),sQuery(id+"F0.wireOp",EDGE,"E107"),sQuery(id+"F0.wireOp",EDGE,"E108"),sQuery(id+"F0.wireOp",EDGE,"E109"),sQuery(id+"F0.wireOp",EDGE,"E110"),sQuery(id+"F0.wireOp",EDGE,"E111"),sQuery(id+"F0.wireOp",EDGE,"E112"),sQuery(id+"F0.wireOp",EDGE,"E113"),sQuery(id+"F0.wireOp",EDGE,"E114"),sQuery(id+"F0.wireOp",EDGE,"E115"),sQuery(id+"F0.wireOp",EDGE,"E116"),sQuery(id+"F0.wireOp",EDGE,"E117"),sQuery(id+"F0.wireOp",EDGE,"E118"),sQuery(id+"F0.wireOp",EDGE,"E119"),sQuery(id+"F0.wireOp",EDGE,"E120"),sQuery(id+"F0.wireOp",EDGE,"E121"),sQuery(id+"F0.wireOp",EDGE,"E122"),sQuery(id+"F0.wireOp",EDGE,"E123"),sQuery(id+"F0.wireOp",EDGE,"E124"),sQuery(id+"F0.wireOp",EDGE,"E125"),sQuery(id+"F0.wireOp",EDGE,"E126"),sQuery(id+"F0.wireOp",EDGE,"E127"),sQuery(id+"F0.wireOp",EDGE,"E128"),sQuery(id+"F0.wireOp",EDGE,"E129"),sQuery(id+"F0.wireOp",EDGE,"E130"),sQuery(id+"F0.wireOp",EDGE,"E131"),sQuery(id+"F0.wireOp",EDGE,"E132"),sQuery(id+"F0.wireOp",EDGE,"E133"),sQuery(id+"F0.wireOp",EDGE,"E134"),sQuery(id+"F0.wireOp",EDGE,"E135"),sQuery(id+"F0.wireOp",EDGE,"E136"),sQuery(id+"F0.wireOp",EDGE,"E137"),sQuery(id+"F0.wireOp",EDGE,"E138"),sQuery(id+"F0.wireOp",EDGE,"E139"),sQuery(id+"F0.wireOp",EDGE,"E140"),sQuery(id+"F0.wireOp",EDGE,"E141"),sQuery(id+"F0.wireOp",EDGE,"E142"),sQuery(id+"F0.wireOp",EDGE,"E143"),sQuery(id+"F0.wireOp",EDGE,"E144"),sQuery(id+"F0.wireOp",EDGE,"E145"),sQuery(id+"F0.wireOp",EDGE,"E146"),sQuery(id+"F0.wireOp",EDGE,"E147"),sQuery(id+"F0.wireOp",EDGE,"E148"),sQuery(id+"F0.wireOp",EDGE,"E149"),sQuery(id+"F0.wireOp",EDGE,"E150"),sQuery(id+"F0.wireOp",EDGE,"E151"),sQuery(id+"F0.wireOp",EDGE,"E152"),sQuery(id+"F0.wireOp",EDGE,"E153"),sQuery(id+"F0.wireOp",EDGE,"E154"),sQuery(id+"F0.wireOp",EDGE,"E155"),sQuery(id+"F0.wireOp",EDGE,"E156"),sQuery(id+"F0.wireOp",EDGE,"E157"),sQuery(id+"F0.wireOp",EDGE,"E158"),sQuery(id+"F0.wireOp",EDGE,"E159"),sQuery(id+"F0.wireOp",EDGE,"E160"),sQuery(id+"F0.wireOp",EDGE,"E161"),sQuery(id+"F0.wireOp",EDGE,"E162"),sQuery(id+"F0.wireOp",EDGE,"E163"),sQuery(id+"F0.wireOp",EDGE,"E164"),sQuery(id+"F0.wireOp",EDGE,"E165"),sQuery(id+"F0.wireOp",EDGE,"E166"),sQuery(id+"F0.wireOp",EDGE,"E167"),sQuery(id+"F0.wireOp",EDGE,"E168"),sQuery(id+"F0.wireOp",EDGE,"E169"),sQuery(id+"F0.wireOp",EDGE,"E170"),sQuery(id+"F0.wireOp",EDGE,"E171"),sQuery(id+"F0.wireOp",EDGE,"E172"),sQuery(id+"F0.wireOp",EDGE,"E173"),sQuery(id+"F0.wireOp",EDGE,"E174"),sQuery(id+"F0.wireOp",EDGE,"E175"),sQuery(id+"F0.wireOp",EDGE,"E176"),sQuery(id+"F0.wireOp",EDGE,"E177"),sQuery(id+"F0.wireOp",EDGE,"E178"),sQuery(id+"F0.wireOp",EDGE,"E179"),sQuery(id+"F0.wireOp",EDGE,"E180"),sQuery(id+"F0.wireOp",EDGE,"E181"),sQuery(id+"F0.wireOp",EDGE,"E182"),sQuery(id+"F0.wireOp",EDGE,"E183"),sQuery(id+"F0.wireOp",EDGE,"E184"),sQuery(id+"F0.wireOp",EDGE,"E185"),sQuery(id+"F0.wireOp",EDGE,"E186"),sQuery(id+"F0.wireOp",EDGE,"E187"),sQuery(id+"F0.wireOp",EDGE,"E188"),sQuery(id+"F0.wireOp",EDGE,"E189"),sQuery(id+"F0.wireOp",EDGE,"E190"),sQuery(id+"F0.wireOp",EDGE,"E191"),sQuery(id+"F0.wireOp",EDGE,"E192"),sQuery(id+"F0.wireOp",EDGE,"E193"),sQuery(id+"F0.wireOp",EDGE,"E194"),sQuery(id+"F0.wireOp",EDGE,"E195"),sQuery(id+"F0.wireOp",EDGE,"E196"),sQuery(id+"F0.wireOp",EDGE,"E197"),sQuery(id+"F0.wireOp",EDGE,"E198"),sQuery(id+"F0.wireOp",EDGE,"E199"),sQuery(id+"F0.wireOp",EDGE,"E200"),sQuery(id+"F0.wireOp",EDGE,"E201"),sQuery(id+"F0.wireOp",EDGE,"E202"),sQuery(id+"F0.wireOp",EDGE,"E203"),sQuery(id+"F0.wireOp",EDGE,"E204"),sQuery(id+"F0.wireOp",EDGE,"E205"),sQuery(id+"F0.wireOp",EDGE,"E206"),sQuery(id+"F0.wireOp",EDGE,"E207"),sQuery(id+"F0.wireOp",EDGE,"E208"),sQuery(id+"F0.wireOp",EDGE,"E209"),sQuery(id+"F0.wireOp",EDGE,"E210"),sQuery(id+"F0.wireOp",EDGE,"E211"),sQuery(id+"F0.wireOp",EDGE,"E212"),sQuery(id+"F0.wireOp",EDGE,"E213"),sQuery(id+"F0.wireOp",EDGE,"E214"),sQuery(id+"F0.wireOp",EDGE,"E215"),sQuery(id+"F0.wireOp",EDGE,"E216"),sQuery(id+"F0.wireOp",EDGE,"E217"),sQuery(id+"F0.wireOp",EDGE,"E218"),sQuery(id+"F0.wireOp",EDGE,"E219"),sQuery(id+"F0.wireOp",EDGE,"E220"),sQuery(id+"F0.wireOp",EDGE,"E221"),sQuery(id+"F0.wireOp",EDGE,"E222"),sQuery(id+"F0.wireOp",EDGE,"E223"),sQuery(id+"F0.wireOp",EDGE,"E224"),sQuery(id+"F0.wireOp",EDGE,"E225"),sQuery(id+"F0.wireOp",EDGE,"E226"),sQuery(id+"F0.wireOp",EDGE,"E227"),sQuery(id+"F0.wireOp",EDGE,"E228"),sQuery(id+"F0.wireOp",EDGE,"E229"),sQuery(id+"F0.wireOp",EDGE,"E230"),sQuery(id+"F0.wireOp",EDGE,"E231"),sQuery(id+"F0.wireOp",EDGE,"E244"),sQuery(id+"F0.wireOp",EDGE,"E245"),sQuery(id+"F0.wireOp",EDGE,"E246"),sQuery(id+"F0.wireOp",EDGE,"E247"),sQuery(id+"F0.wireOp",EDGE,"E248"),sQuery(id+"F0.wireOp",EDGE,"E249"),sQuery(id+"F0.wireOp",EDGE,"E250"),sQuery(id+"F0.wireOp",EDGE,"E251"),sQuery(id+"F0.wireOp",EDGE,"E252"),sQuery(id+"F0.wireOp",EDGE,"E253"),sQuery(id+"F0.wireOp",EDGE,"E254"),sQuery(id+"F0.wireOp",EDGE,"E255"),sQuery(id+"F0.wireOp",EDGE,"E256"),sQuery(id+"F0.wireOp",EDGE,"E257"),sQuery(id+"F0.wireOp",EDGE,"E258"),sQuery(id+"F0.wireOp",EDGE,"E259"),sQuery(id+"F0.wireOp",EDGE,"E260"),sQuery(id+"F0.wireOp",EDGE,"E261"),sQuery(id+"F0.wireOp",EDGE,"E262"),sQuery(id+"F0.wireOp",EDGE,"E291"),sQuery(id+"F0.wireOp",EDGE,"E292"),sQuery(id+"F0.wireOp",EDGE,"E345"),sQuery(id+"F0.wireOp",EDGE,"E346"),sQuery(id+"F0.wireOp",EDGE,"E347"),sQuery(id+"F0.wireOp",EDGE,"E348"),sQuery(id+"F0.wireOp",EDGE,"E349"),sQuery(id+"F0.wireOp",EDGE,"E350"),sQuery(id+"F0.wireOp",EDGE,"E351"),sQuery(id+"F0.wireOp",EDGE,"E352"),sQuery(id+"F0.wireOp",EDGE,"E353")])]});
            var Q5;
            Q5=sQuery(id+"F1.wireOp",VERTEX,"E368.middle");
            transform(context, id + "F4", {"entities" : qUnion([Q0, Q1, Q2, Q3, Q4]), "transformType" : TransformType.SCALE_UNIFORMLY, "scale" : .1, "scalePoint" : qUnion([Q5]), "makeCopy" : false});
        }
    });
